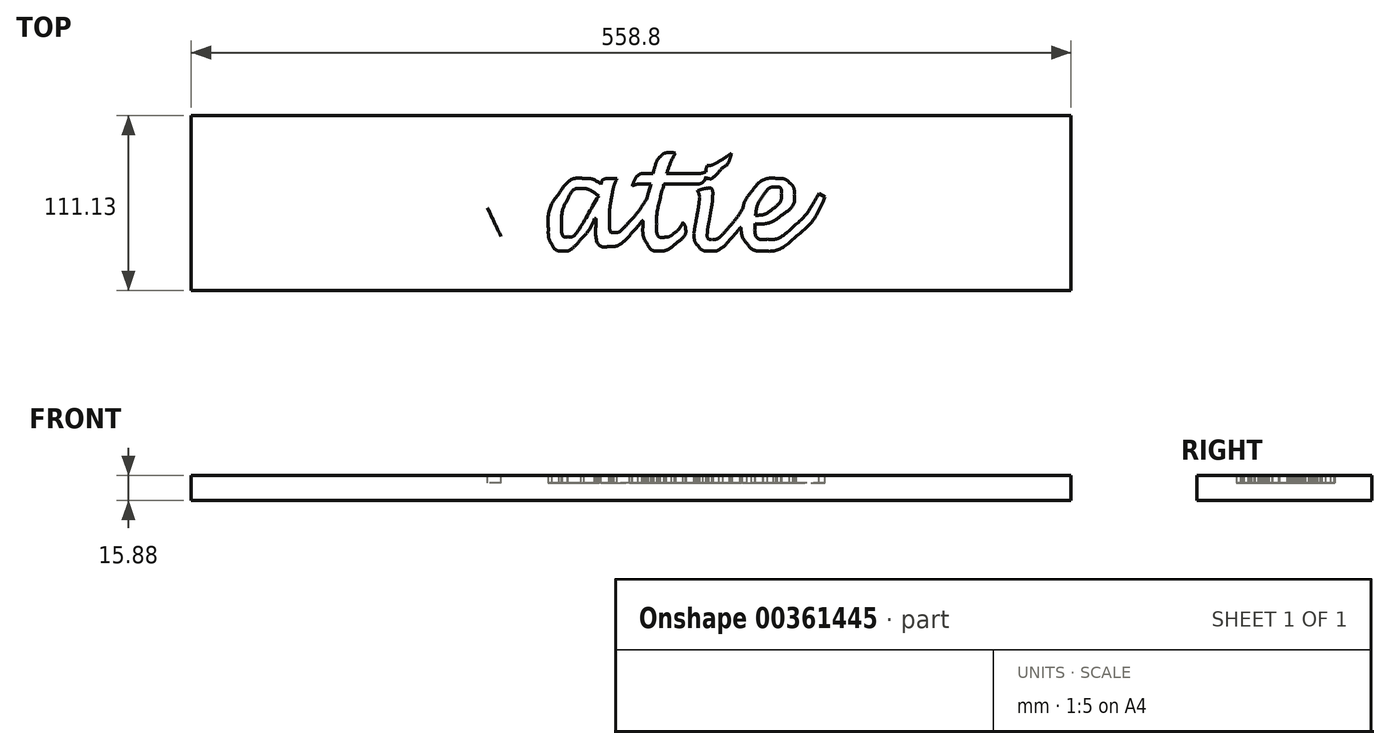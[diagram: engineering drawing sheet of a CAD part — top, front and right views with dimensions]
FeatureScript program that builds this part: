
annotation { "Feature Type Name" : "Feature", "Feature Type Description" : "" }
export const myFeature = defineFeature(function(context is Context, id is Id, definition is map)
    precondition{}
    {
        {
            var Q0;
            Q0=qCreatedBy(makeId("Top.planeOp"),FACE);
            var sketch = newSketch(context, id + "F0", { "sketchPlane" : qUnion([Q0])});
            skLineSegment(sketch, "E0.bottom", {"start": v(12.7, 0) * mm, "end": v(546.1, 0) * mm});
            skLineSegment(sketch, "E0.top", {"start": v(12.7, 609.6) * mm, "end": v(546.1, 609.6) * mm});
            skLineSegment(sketch, "E0.left", {"start": v(0, 12.7) * mm, "end": v(0, 596.9) * mm});
            skLineSegment(sketch, "E0.right", {"start": v(558.8, 12.7) * mm, "end": v(558.8, 596.9) * mm});
            skPoint(sketch, "E1.visualSharp", {"position": v(0, 609.6) * mm});
            skArc(sketch, "E1.filletArc", {"start": v(12.7, 609.6) * mm, "mid": v(3.72, 605.88) * mm, "end": v(0, 596.9) * mm});
            skPoint(sketch, "E2.visualSharp", {"position": v(0, 0) * mm});
            skArc(sketch, "E2.filletArc", {"start": v(0, 12.7) * mm, "mid": v(3.72, 3.72) * mm, "end": v(12.7, 0) * mm});
            skPoint(sketch, "E3.visualSharp", {"position": v(558.8, 0) * mm});
            skArc(sketch, "E3.filletArc", {"start": v(546.1, 0) * mm, "mid": v(555.08, 3.72) * mm, "end": v(558.8, 12.7) * mm});
            skPoint(sketch, "E4.visualSharp", {"position": v(558.8, 609.6) * mm});
            skArc(sketch, "E4.filletArc", {"start": v(558.8, 596.9) * mm, "mid": v(555.08, 605.88) * mm, "end": v(546.1, 609.6) * mm});
            skSolve(sketch);
        }
        {
            var Q0;
            Q0=makeQuery(id+"F0.imprint","IMPRINT",FACE,{"disambiguationData":[TD([[makeQuery(id+"F0.imprint","IMPRINT",EDGE,{"derivedFrom":sQuery(id+"F0.wireOp",EDGE,"E0.bottom")}),1.0]])]});
            extrude(context, id + "F1", {"entities" : qUnion([Q0]), "depth" : 15.88 * mm});
        }
        {
            var Q0;
            Q0=makeQuery(id+"F1.opExtrude","CAP_FACE",FACE,{"disambiguationData":[OSD([sQuery(id+"F0.wireOp",EDGE,"E0.bottom"),sQuery(id+"F0.wireOp",EDGE,"E0.top"),sQuery(id+"F0.wireOp",EDGE,"E0.left"),sQuery(id+"F0.wireOp",EDGE,"E0.right"),sQuery(id+"F0.wireOp",EDGE,"E1.filletArc"),sQuery(id+"F0.wireOp",EDGE,"E2.filletArc"),sQuery(id+"F0.wireOp",EDGE,"E3.filletArc"),sQuery(id+"F0.wireOp",EDGE,"E4.filletArc")])],"isStart":false});
            var sketch = newSketch(context, id + "F2", { "sketchPlane" : qUnion([Q0])});
            skFitSpline(sketch, "E5", {"points": [v(247.46, 485.02) * mm, v(244.22, 485.02) * mm, v(241.38, 482.73) * mm, v(238.94, 478.15) * mm]});
            skFitSpline(sketch, "E6", {"points": [v(238.94, 478.15) * mm, v(236.48, 473.56) * mm, v(235.26, 468.05) * mm, v(235.26, 461.6) * mm]});
            skFitSpline(sketch, "E7", {"points": [v(235.26, 461.6) * mm, v(235.26, 456.87) * mm, v(236.54, 454.5) * mm, v(239.12, 454.5) * mm]});
            skFitSpline(sketch, "E8", {"points": [v(239.12, 454.5) * mm, v(242.2, 454.5) * mm, v(248.34, 462.57) * mm, v(257.6, 478.7) * mm]});
            skFitSpline(sketch, "E9", {"points": [v(257.6, 478.7) * mm, v(257.73, 478.94) * mm, v(258.18, 479.46) * mm, v(258.91, 480.26) * mm]});
            skFitSpline(sketch, "E10", {"points": [v(258.91, 480.26) * mm, v(254.36, 483.44) * mm, v(250.54, 485.02) * mm, v(247.46, 485.02) * mm]});
            skFitSpline(sketch, "E11", {"points": [v(371.38, 485.98) * mm, v(368.47, 485.98) * mm, v(365.74, 484.16) * mm, v(363.18, 480.52) * mm]});
            skFitSpline(sketch, "E12", {"points": [v(363.18, 480.52) * mm, v(360.62, 476.88) * mm, v(359.03, 472.72) * mm, v(358.4, 468.06) * mm]});
            skFitSpline(sketch, "E13", {"points": [v(358.4, 468.06) * mm, v(362.59, 468.32) * mm, v(366.35, 469.82) * mm, v(369.66, 472.53) * mm]});
            skFitSpline(sketch, "E14", {"points": [v(369.66, 472.53) * mm, v(372.98, 475.24) * mm, v(374.64, 478.32) * mm, v(374.64, 481.78) * mm]});
            skFitSpline(sketch, "E15", {"points": [v(374.64, 481.78) * mm, v(374.64, 484.58) * mm, v(373.55, 485.98) * mm, v(371.38, 485.98) * mm]});
            skFitSpline(sketch, "E16", {"points": [v(372.25, 491.45) * mm, v(375.43, 491.45) * mm, v(378, 490.53) * mm, v(379.95, 488.68) * mm]});
            skFitSpline(sketch, "E17", {"points": [v(379.95, 488.68) * mm, v(381.9, 486.84) * mm, v(382.89, 484.38) * mm, v(382.89, 481.3) * mm]});
            skFitSpline(sketch, "E18", {"points": [v(382.89, 481.3) * mm, v(382.89, 476.36) * mm, v(380.3, 472.02) * mm, v(375.12, 468.3) * mm]});
            skFitSpline(sketch, "E19", {"points": [v(375.12, 468.3) * mm, v(369.94, 464.57) * mm, v(364.27, 462.7) * mm, v(358.12, 462.7) * mm]});
            skFitSpline(sketch, "E20", {"points": [v(358.12, 462.7) * mm, v(358.12, 456.15) * mm, v(360.76, 452.87) * mm, v(366.01, 452.87) * mm]});
            skFitSpline(sketch, "E21", {"points": [v(366.01, 452.87) * mm, v(370.84, 452.87) * mm, v(376.2, 455.49) * mm, v(382.13, 460.74) * mm]});
            skFitSpline(sketch, "E22", {"points": [v(382.13, 460.74) * mm, v(388.04, 465.98) * mm, v(393.52, 473.06) * mm, v(398.54, 481.95) * mm]});
            skFitSpline(sketch, "E23", {"points": [v(402.5, 479.62) * mm, v(397.84, 469.55) * mm, v(391.82, 461.33) * mm, v(384.42, 454.98) * mm]});
            skFitSpline(sketch, "E24", {"points": [v(384.42, 454.98) * mm, v(377.03, 448.62) * mm, v(369.98, 445.45) * mm, v(363.3, 445.45) * mm]});
            skFitSpline(sketch, "E25", {"points": [v(363.3, 445.45) * mm, v(358.9, 445.45) * mm, v(355.42, 447.05) * mm, v(352.87, 450.22) * mm]});
            skFitSpline(sketch, "E26", {"points": [v(352.87, 450.22) * mm, v(350.64, 453) * mm, v(349.4, 456.61) * mm, v(349.1, 461.08) * mm]});
            skFitSpline(sketch, "E27", {"points": [v(349.1, 461.08) * mm, v(347.32, 458.56) * mm, v(345.51, 456.33) * mm, v(343.7, 454.35) * mm]});
            skFitSpline(sketch, "E28", {"points": [v(343.7, 454.35) * mm, v(338.24, 448.42) * mm, v(333.27, 445.45) * mm, v(328.8, 445.45) * mm]});
            skFitSpline(sketch, "E29", {"points": [v(328.8, 445.45) * mm, v(325.99, 445.45) * mm, v(323.71, 446.48) * mm, v(322, 448.54) * mm]});
            skFitSpline(sketch, "E30", {"points": [v(322, 448.54) * mm, v(320.27, 450.6) * mm, v(319.41, 453.3) * mm, v(319.41, 456.62) * mm]});
            skFitSpline(sketch, "E31", {"points": [v(319.41, 456.62) * mm, v(319.41, 457.85) * mm, v(319.64, 459.77) * mm, v(320.12, 462.36) * mm]});
            skLineSegment(sketch, "E32", {"start": v(398.54, 481.95) * mm, "end": v(402.5, 479.62) * mm});
            skLineSegment(sketch, "E33", {"start": v(402.5, 479.62) * mm, "end": v(398.54, 481.95) * mm});
            skFitSpline(sketch, "E34", {"points": [v(320.89, 466.68) * mm, v(322, 472.85) * mm, v(322.57, 477.15) * mm, v(322.57, 479.6) * mm]});
            skFitSpline(sketch, "E35", {"points": [v(322.57, 479.6) * mm, v(322.57, 480.87) * mm, v(322.18, 482.24) * mm, v(321.4, 483.7) * mm]});
            skFitSpline(sketch, "E36", {"points": [v(321.4, 483.7) * mm, v(324.84, 484.7) * mm, v(326.97, 485.22) * mm, v(327.78, 485.22) * mm]});
            skFitSpline(sketch, "E37", {"points": [v(327.78, 485.22) * mm, v(329.99, 485.22) * mm, v(331.1, 483.6) * mm, v(331.1, 480.35) * mm]});
            skFitSpline(sketch, "E38", {"points": [v(331.1, 480.35) * mm, v(331.1, 478.32) * mm, v(330.76, 475.38) * mm, v(330.07, 471.54) * mm]});
            skLineSegment(sketch, "E39", {"start": v(320.12, 462.36) * mm, "end": v(320.89, 466.68) * mm});
            skLineSegment(sketch, "E40", {"start": v(320.89, 466.68) * mm, "end": v(320.12, 462.36) * mm});
            skFitSpline(sketch, "E41", {"points": [v(328.7, 463.92) * mm, v(328.05, 460.32) * mm, v(327.73, 458) * mm, v(327.73, 456.92) * mm]});
            skFitSpline(sketch, "E42", {"points": [v(327.73, 456.92) * mm, v(327.73, 454.22) * mm, v(328.7, 452.87) * mm, v(330.64, 452.87) * mm]});
            skFitSpline(sketch, "E43", {"points": [v(330.64, 452.87) * mm, v(333.34, 452.87) * mm, v(337.06, 455.56) * mm, v(341.8, 460.93) * mm]});
            skFitSpline(sketch, "E44", {"points": [v(341.8, 460.93) * mm, v(344.6, 464.12) * mm, v(347.4, 467.87) * mm, v(350.2, 472.2) * mm]});
            skFitSpline(sketch, "E45", {"points": [v(350.2, 472.2) * mm, v(351.28, 476.24) * mm, v(353.16, 479.88) * mm, v(355.83, 483.14) * mm]});
            skFitSpline(sketch, "E46", {"points": [v(355.83, 483.14) * mm, v(360.35, 488.68) * mm, v(365.83, 491.45) * mm, v(372.25, 491.45) * mm]});
            skLineSegment(sketch, "E47", {"start": v(330.07, 471.54) * mm, "end": v(328.7, 463.92) * mm});
            skLineSegment(sketch, "E48", {"start": v(328.7, 463.92) * mm, "end": v(330.07, 471.54) * mm});
            skFitSpline(sketch, "E49", {"points": [v(305.1, 507.84) * mm, v(305.33, 507.84) * mm, v(306.14, 507.78) * mm, v(307.5, 507.65) * mm]});
            skFitSpline(sketch, "E50", {"points": [v(307.5, 507.65) * mm, v(305.64, 504.33) * mm, v(303.76, 499.96) * mm, v(301.86, 494.56) * mm]});
            skFitSpline(sketch, "E51", {"points": [v(319.5, 494.56) * mm, v(322.22, 494.56) * mm, v(324.64, 494.92) * mm, v(326.74, 495.67) * mm]});
            skFitSpline(sketch, "E52", {"points": [v(326.74, 495.67) * mm, v(326.87, 497.05) * mm, v(327.2, 498.41) * mm, v(327.69, 499.77) * mm]});
            skLineSegment(sketch, "E53", {"start": v(301.86, 494.56) * mm, "end": v(319.5, 494.56) * mm});
            skLineSegment(sketch, "E54", {"start": v(319.5, 494.56) * mm, "end": v(301.86, 494.56) * mm});
            skFitSpline(sketch, "E55", {"points": [v(328.67, 499.72) * mm, v(330.08, 499.79) * mm, v(332.2, 500.64) * mm, v(335.04, 502.28) * mm]});
            skFitSpline(sketch, "E56", {"points": [v(335.04, 502.28) * mm, v(337.9, 503.93) * mm, v(340.52, 505.68) * mm, v(342.94, 507.52) * mm]});
            skFitSpline(sketch, "E57", {"points": [v(342.94, 507.52) * mm, v(341.85, 503.08) * mm, v(340.03, 500.06) * mm, v(337.5, 498.48) * mm]});
            skFitSpline(sketch, "E58", {"points": [v(337.5, 498.48) * mm, v(333.26, 493.7) * mm, v(330.34, 491.32) * mm, v(328.76, 491.32) * mm]});
            skFitSpline(sketch, "E59", {"points": [v(328.76, 491.32) * mm, v(327.76, 491.32) * mm, v(327.1, 491.79) * mm, v(326.85, 492.72) * mm]});
            skFitSpline(sketch, "E60", {"points": [v(326.85, 492.72) * mm, v(326.33, 491.05) * mm, v(325.73, 489.92) * mm, v(325.02, 489.33) * mm]});
            skFitSpline(sketch, "E61", {"points": [v(325.02, 489.33) * mm, v(323.92, 488.4) * mm, v(321.98, 487.93) * mm, v(319.18, 487.93) * mm]});
            skLineSegment(sketch, "E62", {"start": v(327.69, 499.77) * mm, "end": v(328.67, 499.72) * mm});
            skLineSegment(sketch, "E63", {"start": v(328.67, 499.72) * mm, "end": v(327.69, 499.77) * mm});
            skFitSpline(sketch, "E64", {"points": [v(300.17, 487.93) * mm, v(300.04, 487.44) * mm, v(299.9, 486.92) * mm, v(299.75, 486.38) * mm]});
            skFitSpline(sketch, "E65", {"points": [v(299.75, 486.38) * mm, v(296.99, 475.84) * mm, v(295.6, 467.88) * mm, v(295.6, 462.47) * mm]});
            skFitSpline(sketch, "E66", {"points": [v(295.6, 462.47) * mm, v(295.6, 456.94) * mm, v(297.3, 454.18) * mm, v(300.68, 454.18) * mm]});
            skFitSpline(sketch, "E67", {"points": [v(300.68, 454.18) * mm, v(302.53, 454.18) * mm, v(304.57, 455.1) * mm, v(306.8, 456.9) * mm]});
            skFitSpline(sketch, "E68", {"points": [v(306.8, 456.9) * mm, v(309.05, 458.71) * mm, v(310.85, 460.91) * mm, v(312.2, 463.5) * mm]});
            skFitSpline(sketch, "E69", {"points": [v(312.2, 463.5) * mm, v(313.35, 461.8) * mm, v(313.92, 460.42) * mm, v(313.92, 459.33) * mm]});
            skFitSpline(sketch, "E70", {"points": [v(313.92, 459.33) * mm, v(313.92, 456.5) * mm, v(311.92, 453.5) * mm, v(307.92, 450.28) * mm]});
            skFitSpline(sketch, "E71", {"points": [v(307.92, 450.28) * mm, v(303.9, 447.06) * mm, v(300.24, 445.45) * mm, v(296.9, 445.45) * mm]});
            skFitSpline(sketch, "E72", {"points": [v(296.9, 445.45) * mm, v(293.88, 445.45) * mm, v(291.42, 446.93) * mm, v(289.56, 449.9) * mm]});
            skFitSpline(sketch, "E73", {"points": [v(289.56, 449.9) * mm, v(287.7, 452.87) * mm, v(286.76, 456.65) * mm, v(286.76, 461.23) * mm]});
            skFitSpline(sketch, "E74", {"points": [v(286.76, 461.23) * mm, v(286.76, 462.58) * mm, v(286.84, 464.08) * mm, v(287.02, 465.75) * mm]});
            skFitSpline(sketch, "E75", {"points": [v(287.02, 465.75) * mm, v(284.81, 462.56) * mm, v(282.47, 459.69) * mm, v(280.01, 457.13) * mm]});
            skFitSpline(sketch, "E76", {"points": [v(280.01, 457.13) * mm, v(274.37, 451.28) * mm, v(269.48, 448.36) * mm, v(265.31, 448.36) * mm]});
            skFitSpline(sketch, "E77", {"points": [v(265.31, 448.36) * mm, v(259.81, 448.36) * mm, v(257.07, 453.3) * mm, v(257.07, 463.23) * mm]});
            skFitSpline(sketch, "E78", {"points": [v(257.07, 463.23) * mm, v(257.07, 465.2) * mm, v(257.14, 467.57) * mm, v(257.28, 470.32) * mm]});
            skFitSpline(sketch, "E79", {"points": [v(257.28, 470.32) * mm, v(255.19, 463.64) * mm, v(251.91, 457.83) * mm, v(247.46, 452.87) * mm]});
            skFitSpline(sketch, "E80", {"points": [v(247.46, 452.87) * mm, v(242.99, 447.92) * mm, v(239.04, 445.45) * mm, v(235.6, 445.45) * mm]});
            skFitSpline(sketch, "E81", {"points": [v(235.6, 445.45) * mm, v(232.88, 445.45) * mm, v(230.72, 446.77) * mm, v(229.15, 449.4) * mm]});
            skFitSpline(sketch, "E82", {"points": [v(229.15, 449.4) * mm, v(227.56, 452.05) * mm, v(226.77, 455.51) * mm, v(226.77, 459.78) * mm]});
            skFitSpline(sketch, "E83", {"points": [v(226.77, 459.78) * mm, v(226.77, 468.13) * mm, v(229.03, 475.5) * mm, v(233.56, 481.87) * mm]});
            skFitSpline(sketch, "E84", {"points": [v(233.56, 481.87) * mm, v(238.09, 488.26) * mm, v(243.35, 491.45) * mm, v(249.38, 491.45) * mm]});
            skFitSpline(sketch, "E85", {"points": [v(249.38, 491.45) * mm, v(253.01, 491.45) * mm, v(256.66, 490.21) * mm, v(260.33, 487.76) * mm]});
            skFitSpline(sketch, "E86", {"points": [v(260.33, 487.76) * mm, v(260.86, 490.19) * mm, v(263.48, 491.4) * mm, v(268.16, 491.4) * mm]});
            skFitSpline(sketch, "E87", {"points": [v(268.16, 491.4) * mm, v(268.26, 491.4) * mm, v(268.96, 491.37) * mm, v(270.27, 491.3) * mm]});
            skFitSpline(sketch, "E88", {"points": [v(270.27, 491.3) * mm, v(268.9, 488.33) * mm, v(267.89, 484.93) * mm, v(267.2, 481.1) * mm]});
            skLineSegment(sketch, "E89", {"start": v(319.18, 487.93) * mm, "end": v(300.17, 487.93) * mm});
            skLineSegment(sketch, "E90", {"start": v(300.17, 487.93) * mm, "end": v(319.18, 487.93) * mm});
            skFitSpline(sketch, "E91", {"points": [v(266.62, 477.77) * mm, v(265.96, 474.15) * mm, v(265.63, 469.88) * mm, v(265.63, 464.94) * mm]});
            skFitSpline(sketch, "E92", {"points": [v(265.63, 464.94) * mm, v(265.63, 459.77) * mm, v(266.57, 457.18) * mm, v(268.44, 457.18) * mm]});
            skFitSpline(sketch, "E93", {"points": [v(268.44, 457.18) * mm, v(270.76, 457.18) * mm, v(274.05, 459.48) * mm, v(278.32, 464.1) * mm]});
            skFitSpline(sketch, "E94", {"points": [v(278.32, 464.1) * mm, v(281.96, 468.04) * mm, v(285.66, 473) * mm, v(289.42, 478.98) * mm]});
            skFitSpline(sketch, "E95", {"points": [v(289.42, 478.98) * mm, v(289.7, 480.18) * mm, v(290, 481.4) * mm, v(290.32, 482.69) * mm]});
            skLineSegment(sketch, "E96", {"start": v(267.2, 481.1) * mm, "end": v(266.62, 477.77) * mm});
            skLineSegment(sketch, "E97", {"start": v(266.62, 477.77) * mm, "end": v(267.2, 481.1) * mm});
            skFitSpline(sketch, "E98", {"points": [v(286.65, 487.93) * mm, v(284.3, 487.93) * mm, v(282.1, 487.54) * mm, v(280.04, 486.76) * mm]});
            skFitSpline(sketch, "E99", {"points": [v(280.04, 486.76) * mm, v(281.5, 490.38) * mm, v(282.72, 492.6) * mm, v(283.72, 493.38) * mm]});
            skFitSpline(sketch, "E100", {"points": [v(283.72, 493.38) * mm, v(284.71, 494.16) * mm, v(286.34, 494.56) * mm, v(288.6, 494.56) * mm]});
            skLineSegment(sketch, "E101", {"start": v(290.32, 482.69) * mm, "end": v(291.82, 487.93) * mm});
            skLineSegment(sketch, "E102", {"start": v(291.82, 487.93) * mm, "end": v(286.65, 487.93) * mm});
            skFitSpline(sketch, "E103", {"points": [v(293.99, 497.12) * mm, v(295.02, 501) * mm, v(296.33, 503.76) * mm, v(297.95, 505.4) * mm]});
            skFitSpline(sketch, "E104", {"points": [v(297.95, 505.4) * mm, v(299.55, 507.03) * mm, v(301.94, 507.84) * mm, v(305.1, 507.84) * mm]});
            skLineSegment(sketch, "E105", {"start": v(288.6, 494.56) * mm, "end": v(293.33, 494.56) * mm});
            skLineSegment(sketch, "E106", {"start": v(293.33, 494.56) * mm, "end": v(293.99, 497.12) * mm});
            skFitSpline(sketch, "E107", {"points": [v(178.41, 506.2) * mm, v(181.96, 506.2) * mm, v(186.85, 506.6) * mm, v(193.08, 507.4) * mm]});
            skFitSpline(sketch, "E108", {"points": [v(188.04, 478.85) * mm, v(200.42, 488.81) * mm, v(207.85, 498.44) * mm, v(210.33, 507.7) * mm]});
            skFitSpline(sketch, "E109", {"points": [v(210.33, 507.7) * mm, v(214.42, 505.56) * mm, v(216.46, 503.26) * mm, v(216.46, 500.79) * mm]});
            skFitSpline(sketch, "E110", {"points": [v(216.46, 500.79) * mm, v(216.46, 499.37) * mm, v(213.98, 496.13) * mm, v(209, 491.1) * mm]});
            skFitSpline(sketch, "E111", {"points": [v(209, 491.1) * mm, v(204.02, 486.08) * mm, v(199.1, 481.73) * mm, v(194.23, 478.07) * mm]});
            skFitSpline(sketch, "E112", {"points": [v(194.23, 478.07) * mm, v(198.39, 469.54) * mm, v(202.46, 462.52) * mm, v(206.43, 457.03) * mm]});
            skFitSpline(sketch, "E113", {"points": [v(206.43, 457.03) * mm, v(210.4, 451.54) * mm, v(213.38, 448.8) * mm, v(215.37, 448.8) * mm]});
            skFitSpline(sketch, "E114", {"points": [v(215.37, 448.8) * mm, v(217.55, 448.8) * mm, v(220.39, 450.27) * mm, v(223.87, 453.22) * mm]});
            skLineSegment(sketch, "E115", {"start": v(193.08, 507.4) * mm, "end": v(188.41, 480.96) * mm});
            skLineSegment(sketch, "E116", {"start": v(188.41, 480.96) * mm, "end": v(193.08, 507.4) * mm});
            skFitSpline(sketch, "E117", {"points": [v(223.98, 451.1) * mm, v(223.98, 449.09) * mm, v(222.68, 446.98) * mm, v(220.08, 444.73) * mm]});
            skFitSpline(sketch, "E118", {"points": [v(220.08, 444.73) * mm, v(217.49, 442.5) * mm, v(214.96, 441.38) * mm, v(212.51, 441.38) * mm]});
            skFitSpline(sketch, "E119", {"points": [v(212.54, 441.4) * mm, v(206.33, 441.4) * mm, v(197.88, 452.52) * mm, v(187.21, 474.77) * mm]});
            skLineSegment(sketch, "E120", {"start": v(223.87, 453.22) * mm, "end": v(223.98, 451.1) * mm});
            skLineSegment(sketch, "E121", {"start": v(223.98, 451.1) * mm, "end": v(223.87, 453.22) * mm});
            skFitSpline(sketch, "E122", {"points": [v(183.9, 454.8) * mm, v(183.48, 452.44) * mm, v(183.27, 450.88) * mm, v(183.27, 450.14) * mm]});
            skFitSpline(sketch, "E123", {"points": [v(183.27, 450.14) * mm, v(183.27, 449.5) * mm, v(183.42, 448.6) * mm, v(183.73, 447.42) * mm]});
            skFitSpline(sketch, "E124", {"points": [v(183.73, 447.42) * mm, v(180.96, 445.82) * mm, v(178.55, 445.01) * mm, v(176.52, 445.01) * mm]});
            skFitSpline(sketch, "E125", {"points": [v(176.52, 445.01) * mm, v(174.84, 445.01) * mm, v(174, 445.83) * mm, v(174, 447.45) * mm]});
            skFitSpline(sketch, "E126", {"points": [v(174, 447.45) * mm, v(174, 448.08) * mm, v(174.25, 449.8) * mm, v(174.74, 452.56) * mm]});
            skLineSegment(sketch, "E127", {"start": v(186.79, 472.34) * mm, "end": v(183.9, 454.8) * mm});
            skLineSegment(sketch, "E128", {"start": v(183.9, 454.8) * mm, "end": v(186.79, 472.34) * mm});
            skFitSpline(sketch, "E129", {"points": [v(183.17, 499.25) * mm, v(181.66, 498.94) * mm, v(180, 498.79) * mm, v(178.17, 498.79) * mm]});
            skFitSpline(sketch, "E130", {"points": [v(178.17, 498.79) * mm, v(174.1, 498.79) * mm, v(171.7, 502.02) * mm, v(170.94, 508.51) * mm]});
            skLineSegment(sketch, "E131", {"start": v(174.74, 452.56) * mm, "end": v(183.17, 499.25) * mm});
            skLineSegment(sketch, "E132", {"start": v(183.17, 499.25) * mm, "end": v(174.74, 452.56) * mm});
            skFitSpline(sketch, "E133", {"points": [v(247.46, 485.02) * mm, v(244.22, 485.02) * mm, v(241.38, 482.73) * mm, v(238.94, 478.15) * mm]});
            skFitSpline(sketch, "E134", {"points": [v(238.94, 478.15) * mm, v(236.48, 473.56) * mm, v(235.26, 468.05) * mm, v(235.26, 461.6) * mm]});
            skFitSpline(sketch, "E135", {"points": [v(235.26, 461.6) * mm, v(235.26, 456.87) * mm, v(236.54, 454.5) * mm, v(239.12, 454.5) * mm]});
            skFitSpline(sketch, "E136", {"points": [v(239.12, 454.5) * mm, v(242.2, 454.5) * mm, v(248.34, 462.57) * mm, v(257.6, 478.7) * mm]});
            skFitSpline(sketch, "E137", {"points": [v(257.6, 478.7) * mm, v(257.73, 478.94) * mm, v(258.18, 479.46) * mm, v(258.91, 480.26) * mm]});
            skFitSpline(sketch, "E138", {"points": [v(258.91, 480.26) * mm, v(254.36, 483.44) * mm, v(250.54, 485.02) * mm, v(247.46, 485.02) * mm]});
            skFitSpline(sketch, "E139", {"points": [v(371.38, 485.98) * mm, v(368.47, 485.98) * mm, v(365.74, 484.16) * mm, v(363.18, 480.52) * mm]});
            skFitSpline(sketch, "E140", {"points": [v(363.18, 480.52) * mm, v(360.62, 476.88) * mm, v(359.03, 472.72) * mm, v(358.4, 468.06) * mm]});
            skFitSpline(sketch, "E141", {"points": [v(358.4, 468.06) * mm, v(362.59, 468.32) * mm, v(366.35, 469.82) * mm, v(369.66, 472.53) * mm]});
            skFitSpline(sketch, "E142", {"points": [v(369.66, 472.53) * mm, v(372.98, 475.24) * mm, v(374.64, 478.32) * mm, v(374.64, 481.78) * mm]});
            skFitSpline(sketch, "E143", {"points": [v(374.64, 481.78) * mm, v(374.64, 484.58) * mm, v(373.55, 485.98) * mm, v(371.38, 485.98) * mm]});
            skFitSpline(sketch, "E144", {"points": [v(372.25, 491.45) * mm, v(375.43, 491.45) * mm, v(378, 490.53) * mm, v(379.95, 488.68) * mm]});
            skFitSpline(sketch, "E145", {"points": [v(379.95, 488.68) * mm, v(381.9, 486.84) * mm, v(382.89, 484.38) * mm, v(382.89, 481.3) * mm]});
            skFitSpline(sketch, "E146", {"points": [v(382.89, 481.3) * mm, v(382.89, 476.36) * mm, v(380.3, 472.02) * mm, v(375.12, 468.3) * mm]});
            skFitSpline(sketch, "E147", {"points": [v(375.12, 468.3) * mm, v(369.94, 464.57) * mm, v(364.27, 462.7) * mm, v(358.12, 462.7) * mm]});
            skFitSpline(sketch, "E148", {"points": [v(358.12, 462.7) * mm, v(358.12, 456.15) * mm, v(360.76, 452.87) * mm, v(366.01, 452.87) * mm]});
            skFitSpline(sketch, "E149", {"points": [v(366.01, 452.87) * mm, v(370.84, 452.87) * mm, v(376.2, 455.49) * mm, v(382.13, 460.74) * mm]});
            skFitSpline(sketch, "E150", {"points": [v(382.13, 460.74) * mm, v(388.04, 465.98) * mm, v(393.52, 473.06) * mm, v(398.54, 481.95) * mm]});
            skFitSpline(sketch, "E151", {"points": [v(402.5, 479.62) * mm, v(397.84, 469.55) * mm, v(391.82, 461.33) * mm, v(384.42, 454.98) * mm]});
            skFitSpline(sketch, "E152", {"points": [v(384.42, 454.98) * mm, v(377.03, 448.62) * mm, v(369.98, 445.45) * mm, v(363.3, 445.45) * mm]});
            skFitSpline(sketch, "E153", {"points": [v(363.3, 445.45) * mm, v(358.9, 445.45) * mm, v(355.42, 447.05) * mm, v(352.87, 450.22) * mm]});
            skFitSpline(sketch, "E154", {"points": [v(352.87, 450.22) * mm, v(350.64, 453) * mm, v(349.4, 456.61) * mm, v(349.1, 461.08) * mm]});
            skFitSpline(sketch, "E155", {"points": [v(349.1, 461.08) * mm, v(347.32, 458.56) * mm, v(345.51, 456.33) * mm, v(343.7, 454.35) * mm]});
            skFitSpline(sketch, "E156", {"points": [v(343.7, 454.35) * mm, v(338.24, 448.42) * mm, v(333.27, 445.45) * mm, v(328.8, 445.45) * mm]});
            skFitSpline(sketch, "E157", {"points": [v(328.8, 445.45) * mm, v(325.99, 445.45) * mm, v(323.71, 446.48) * mm, v(322, 448.54) * mm]});
            skFitSpline(sketch, "E158", {"points": [v(322, 448.54) * mm, v(320.27, 450.6) * mm, v(319.41, 453.3) * mm, v(319.41, 456.62) * mm]});
            skFitSpline(sketch, "E159", {"points": [v(319.41, 456.62) * mm, v(319.41, 457.85) * mm, v(319.64, 459.77) * mm, v(320.12, 462.36) * mm]});
            skFitSpline(sketch, "E160", {"points": [v(320.89, 466.68) * mm, v(322, 472.85) * mm, v(322.57, 477.15) * mm, v(322.57, 479.6) * mm]});
            skFitSpline(sketch, "E161", {"points": [v(322.57, 479.6) * mm, v(322.57, 480.87) * mm, v(322.18, 482.24) * mm, v(321.4, 483.7) * mm]});
            skFitSpline(sketch, "E162", {"points": [v(321.4, 483.7) * mm, v(324.84, 484.7) * mm, v(326.97, 485.22) * mm, v(327.78, 485.22) * mm]});
            skFitSpline(sketch, "E163", {"points": [v(327.78, 485.22) * mm, v(329.99, 485.22) * mm, v(331.1, 483.6) * mm, v(331.1, 480.35) * mm]});
            skFitSpline(sketch, "E164", {"points": [v(331.1, 480.35) * mm, v(331.1, 478.32) * mm, v(330.76, 475.38) * mm, v(330.07, 471.54) * mm]});
            skFitSpline(sketch, "E165", {"points": [v(328.7, 463.92) * mm, v(328.05, 460.32) * mm, v(327.73, 458) * mm, v(327.73, 456.92) * mm]});
            skFitSpline(sketch, "E166", {"points": [v(327.73, 456.92) * mm, v(327.73, 454.22) * mm, v(328.7, 452.87) * mm, v(330.64, 452.87) * mm]});
            skFitSpline(sketch, "E167", {"points": [v(330.64, 452.87) * mm, v(333.34, 452.87) * mm, v(337.06, 455.56) * mm, v(341.8, 460.93) * mm]});
            skFitSpline(sketch, "E168", {"points": [v(341.8, 460.93) * mm, v(344.6, 464.12) * mm, v(347.4, 467.87) * mm, v(350.2, 472.2) * mm]});
            skFitSpline(sketch, "E169", {"points": [v(350.2, 472.2) * mm, v(351.28, 476.24) * mm, v(353.16, 479.88) * mm, v(355.83, 483.14) * mm]});
            skFitSpline(sketch, "E170", {"points": [v(355.83, 483.14) * mm, v(360.35, 488.68) * mm, v(365.83, 491.45) * mm, v(372.25, 491.45) * mm]});
            skFitSpline(sketch, "E171", {"points": [v(305.1, 507.84) * mm, v(305.33, 507.84) * mm, v(306.14, 507.78) * mm, v(307.5, 507.65) * mm]});
            skFitSpline(sketch, "E172", {"points": [v(307.5, 507.65) * mm, v(305.64, 504.33) * mm, v(303.76, 499.96) * mm, v(301.86, 494.56) * mm]});
            skFitSpline(sketch, "E173", {"points": [v(319.5, 494.56) * mm, v(322.22, 494.56) * mm, v(324.64, 494.92) * mm, v(326.74, 495.67) * mm]});
            skFitSpline(sketch, "E174", {"points": [v(326.74, 495.67) * mm, v(326.87, 497.05) * mm, v(327.2, 498.41) * mm, v(327.69, 499.77) * mm]});
            skFitSpline(sketch, "E175", {"points": [v(328.67, 499.72) * mm, v(330.08, 499.79) * mm, v(332.2, 500.64) * mm, v(335.04, 502.28) * mm]});
            skFitSpline(sketch, "E176", {"points": [v(335.04, 502.28) * mm, v(337.9, 503.93) * mm, v(340.52, 505.68) * mm, v(342.94, 507.52) * mm]});
            skFitSpline(sketch, "E177", {"points": [v(342.94, 507.52) * mm, v(341.85, 503.08) * mm, v(340.03, 500.06) * mm, v(337.5, 498.48) * mm]});
            skFitSpline(sketch, "E178", {"points": [v(337.5, 498.48) * mm, v(333.26, 493.7) * mm, v(330.34, 491.32) * mm, v(328.76, 491.32) * mm]});
            skFitSpline(sketch, "E179", {"points": [v(328.76, 491.32) * mm, v(327.76, 491.32) * mm, v(327.1, 491.79) * mm, v(326.85, 492.72) * mm]});
            skFitSpline(sketch, "E180", {"points": [v(326.85, 492.72) * mm, v(326.33, 491.05) * mm, v(325.73, 489.92) * mm, v(325.02, 489.33) * mm]});
            skFitSpline(sketch, "E181", {"points": [v(325.02, 489.33) * mm, v(323.92, 488.4) * mm, v(321.98, 487.93) * mm, v(319.18, 487.93) * mm]});
            skFitSpline(sketch, "E182", {"points": [v(300.17, 487.93) * mm, v(300.04, 487.44) * mm, v(299.9, 486.92) * mm, v(299.75, 486.38) * mm]});
            skFitSpline(sketch, "E183", {"points": [v(299.75, 486.38) * mm, v(296.99, 475.84) * mm, v(295.6, 467.88) * mm, v(295.6, 462.47) * mm]});
            skFitSpline(sketch, "E184", {"points": [v(295.6, 462.47) * mm, v(295.6, 456.94) * mm, v(297.3, 454.18) * mm, v(300.68, 454.18) * mm]});
            skFitSpline(sketch, "E185", {"points": [v(300.68, 454.18) * mm, v(302.53, 454.18) * mm, v(304.57, 455.1) * mm, v(306.8, 456.9) * mm]});
            skFitSpline(sketch, "E186", {"points": [v(306.8, 456.9) * mm, v(309.05, 458.71) * mm, v(310.85, 460.91) * mm, v(312.2, 463.5) * mm]});
            skFitSpline(sketch, "E187", {"points": [v(312.2, 463.5) * mm, v(313.35, 461.8) * mm, v(313.92, 460.42) * mm, v(313.92, 459.33) * mm]});
            skFitSpline(sketch, "E188", {"points": [v(313.92, 459.33) * mm, v(313.92, 456.5) * mm, v(311.92, 453.5) * mm, v(307.92, 450.28) * mm]});
            skFitSpline(sketch, "E189", {"points": [v(307.92, 450.28) * mm, v(303.9, 447.06) * mm, v(300.24, 445.45) * mm, v(296.9, 445.45) * mm]});
            skFitSpline(sketch, "E190", {"points": [v(296.9, 445.45) * mm, v(293.88, 445.45) * mm, v(291.42, 446.93) * mm, v(289.56, 449.9) * mm]});
            skFitSpline(sketch, "E191", {"points": [v(289.56, 449.9) * mm, v(287.7, 452.87) * mm, v(286.76, 456.65) * mm, v(286.76, 461.23) * mm]});
            skFitSpline(sketch, "E192", {"points": [v(286.76, 461.23) * mm, v(286.76, 462.58) * mm, v(286.84, 464.08) * mm, v(287.02, 465.75) * mm]});
            skFitSpline(sketch, "E193", {"points": [v(287.02, 465.75) * mm, v(284.81, 462.56) * mm, v(282.47, 459.69) * mm, v(280.01, 457.13) * mm]});
            skFitSpline(sketch, "E194", {"points": [v(280.01, 457.13) * mm, v(274.37, 451.28) * mm, v(269.48, 448.36) * mm, v(265.31, 448.36) * mm]});
            skFitSpline(sketch, "E195", {"points": [v(265.31, 448.36) * mm, v(259.81, 448.36) * mm, v(257.07, 453.3) * mm, v(257.07, 463.23) * mm]});
            skFitSpline(sketch, "E196", {"points": [v(257.07, 463.23) * mm, v(257.07, 465.2) * mm, v(257.14, 467.57) * mm, v(257.28, 470.32) * mm]});
            skFitSpline(sketch, "E197", {"points": [v(257.28, 470.32) * mm, v(255.19, 463.64) * mm, v(251.91, 457.83) * mm, v(247.46, 452.87) * mm]});
            skFitSpline(sketch, "E198", {"points": [v(247.46, 452.87) * mm, v(242.99, 447.92) * mm, v(239.04, 445.45) * mm, v(235.6, 445.45) * mm]});
            skFitSpline(sketch, "E199", {"points": [v(235.6, 445.45) * mm, v(232.88, 445.45) * mm, v(230.72, 446.77) * mm, v(229.15, 449.4) * mm]});
            skFitSpline(sketch, "E200", {"points": [v(229.15, 449.4) * mm, v(227.56, 452.05) * mm, v(226.77, 455.51) * mm, v(226.77, 459.78) * mm]});
            skFitSpline(sketch, "E201", {"points": [v(226.77, 459.78) * mm, v(226.77, 468.13) * mm, v(229.03, 475.5) * mm, v(233.56, 481.87) * mm]});
            skFitSpline(sketch, "E202", {"points": [v(233.56, 481.87) * mm, v(238.09, 488.26) * mm, v(243.35, 491.45) * mm, v(249.38, 491.45) * mm]});
            skFitSpline(sketch, "E203", {"points": [v(249.38, 491.45) * mm, v(253.01, 491.45) * mm, v(256.66, 490.21) * mm, v(260.33, 487.76) * mm]});
            skFitSpline(sketch, "E204", {"points": [v(260.33, 487.76) * mm, v(260.86, 490.19) * mm, v(263.48, 491.4) * mm, v(268.16, 491.4) * mm]});
            skFitSpline(sketch, "E205", {"points": [v(268.16, 491.4) * mm, v(268.26, 491.4) * mm, v(268.96, 491.37) * mm, v(270.27, 491.3) * mm]});
            skFitSpline(sketch, "E206", {"points": [v(270.27, 491.3) * mm, v(268.9, 488.33) * mm, v(267.89, 484.93) * mm, v(267.2, 481.1) * mm]});
            skFitSpline(sketch, "E207", {"points": [v(266.62, 477.77) * mm, v(265.96, 474.15) * mm, v(265.63, 469.88) * mm, v(265.63, 464.94) * mm]});
            skFitSpline(sketch, "E208", {"points": [v(265.63, 464.94) * mm, v(265.63, 459.77) * mm, v(266.57, 457.18) * mm, v(268.44, 457.18) * mm]});
            skFitSpline(sketch, "E209", {"points": [v(268.44, 457.18) * mm, v(270.76, 457.18) * mm, v(274.05, 459.48) * mm, v(278.32, 464.1) * mm]});
            skFitSpline(sketch, "E210", {"points": [v(278.32, 464.1) * mm, v(281.96, 468.04) * mm, v(285.66, 473) * mm, v(289.42, 478.98) * mm]});
            skFitSpline(sketch, "E211", {"points": [v(289.42, 478.98) * mm, v(289.7, 480.18) * mm, v(290, 481.4) * mm, v(290.32, 482.69) * mm]});
            skFitSpline(sketch, "E212", {"points": [v(286.65, 487.93) * mm, v(284.3, 487.93) * mm, v(282.1, 487.54) * mm, v(280.04, 486.76) * mm]});
            skFitSpline(sketch, "E213", {"points": [v(280.04, 486.76) * mm, v(281.5, 490.38) * mm, v(282.72, 492.6) * mm, v(283.72, 493.38) * mm]});
            skFitSpline(sketch, "E214", {"points": [v(283.72, 493.38) * mm, v(284.71, 494.16) * mm, v(286.34, 494.56) * mm, v(288.6, 494.56) * mm]});
            skFitSpline(sketch, "E215", {"points": [v(293.99, 497.12) * mm, v(295.02, 501) * mm, v(296.33, 503.76) * mm, v(297.95, 505.4) * mm]});
            skFitSpline(sketch, "E216", {"points": [v(297.95, 505.4) * mm, v(299.55, 507.03) * mm, v(301.94, 507.84) * mm, v(305.1, 507.84) * mm]});
            skFitSpline(sketch, "E217", {"points": [v(170.94, 508.51) * mm, v(173.27, 506.97) * mm, v(175.75, 506.2) * mm, v(178.41, 506.2) * mm]});
            skFitSpline(sketch, "E218", {"points": [v(178.41, 506.2) * mm, v(181.96, 506.2) * mm, v(186.85, 506.6) * mm, v(193.08, 507.4) * mm]});
            skFitSpline(sketch, "E219", {"points": [v(188.04, 478.85) * mm, v(200.42, 488.81) * mm, v(207.85, 498.44) * mm, v(210.33, 507.7) * mm]});
            skFitSpline(sketch, "E220", {"points": [v(210.33, 507.7) * mm, v(214.42, 505.56) * mm, v(216.46, 503.26) * mm, v(216.46, 500.79) * mm]});
            skFitSpline(sketch, "E221", {"points": [v(216.46, 500.79) * mm, v(216.46, 499.37) * mm, v(213.98, 496.13) * mm, v(209, 491.1) * mm]});
            skFitSpline(sketch, "E222", {"points": [v(209, 491.1) * mm, v(204.02, 486.08) * mm, v(199.1, 481.73) * mm, v(194.23, 478.07) * mm]});
            skFitSpline(sketch, "E223", {"points": [v(194.23, 478.07) * mm, v(198.39, 469.54) * mm, v(202.46, 462.52) * mm, v(206.43, 457.03) * mm]});
            skFitSpline(sketch, "E224", {"points": [v(206.43, 457.03) * mm, v(210.4, 451.54) * mm, v(213.38, 448.8) * mm, v(215.37, 448.8) * mm]});
            skFitSpline(sketch, "E225", {"points": [v(215.37, 448.8) * mm, v(217.55, 448.8) * mm, v(220.39, 450.27) * mm, v(223.87, 453.22) * mm]});
            skFitSpline(sketch, "E226", {"points": [v(223.98, 451.1) * mm, v(223.98, 449.09) * mm, v(222.68, 446.98) * mm, v(220.08, 444.73) * mm]});
            skFitSpline(sketch, "E227", {"points": [v(220.08, 444.73) * mm, v(217.49, 442.5) * mm, v(214.96, 441.38) * mm, v(212.51, 441.38) * mm]});
            skFitSpline(sketch, "E228", {"points": [v(212.51, 441.38) * mm, v(206.3, 441.4) * mm, v(197.87, 452.53) * mm, v(187.24, 474.8) * mm]});
            skFitSpline(sketch, "E229", {"points": [v(183.9, 454.8) * mm, v(183.48, 452.44) * mm, v(183.27, 450.88) * mm, v(183.27, 450.14) * mm]});
            skFitSpline(sketch, "E230", {"points": [v(183.27, 450.14) * mm, v(183.27, 449.5) * mm, v(183.42, 448.6) * mm, v(183.73, 447.42) * mm]});
            skFitSpline(sketch, "E231", {"points": [v(183.73, 447.42) * mm, v(180.96, 445.82) * mm, v(178.55, 445.01) * mm, v(176.52, 445.01) * mm]});
            skFitSpline(sketch, "E232", {"points": [v(176.52, 445.01) * mm, v(174.84, 445.01) * mm, v(174, 445.83) * mm, v(174, 447.45) * mm]});
            skFitSpline(sketch, "E233", {"points": [v(174, 447.45) * mm, v(174, 448.08) * mm, v(174.25, 449.8) * mm, v(174.74, 452.56) * mm]});
            skFitSpline(sketch, "E234", {"points": [v(183.17, 499.25) * mm, v(181.66, 498.94) * mm, v(180, 498.79) * mm, v(178.17, 498.79) * mm]});
            skFitSpline(sketch, "E235", {"points": [v(178.17, 498.79) * mm, v(174.1, 498.79) * mm, v(171.7, 502.02) * mm, v(170.94, 508.51) * mm]});
            skFitSpline(sketch, "E236", {"points": [v(277.79, 394.65) * mm, v(280.95, 394.65) * mm, v(283.67, 394.04) * mm, v(285.93, 392.83) * mm]});
            skFitSpline(sketch, "E237", {"points": [v(285.93, 392.83) * mm, v(288.2, 391.61) * mm, v(289.33, 390.05) * mm, v(289.33, 388.1) * mm]});
            skFitSpline(sketch, "E238", {"points": [v(289.33, 388.1) * mm, v(289.33, 386.55) * mm, v(288.3, 384.9) * mm, v(286.28, 383.13) * mm]});
            skFitSpline(sketch, "E239", {"points": [v(286.28, 383.13) * mm, v(284.16, 387.16) * mm, v(281.01, 389.18) * mm, v(276.84, 389.18) * mm]});
            skFitSpline(sketch, "E240", {"points": [v(276.84, 389.18) * mm, v(274.08, 389.18) * mm, v(271.82, 388.38) * mm, v(270.07, 386.75) * mm]});
            skFitSpline(sketch, "E241", {"points": [v(270.07, 386.75) * mm, v(268.32, 385.12) * mm, v(267.44, 383.06) * mm, v(267.44, 380.56) * mm]});
            skFitSpline(sketch, "E242", {"points": [v(267.44, 380.56) * mm, v(267.44, 377.66) * mm, v(268.8, 375.02) * mm, v(271.5, 372.69) * mm]});
            skFitSpline(sketch, "E243", {"points": [v(271.5, 372.69) * mm, v(273.4, 373.18) * mm, v(275.11, 373.43) * mm, v(276.63, 373.43) * mm]});
            skFitSpline(sketch, "E244", {"points": [v(276.63, 373.43) * mm, v(278.07, 373.43) * mm, v(279.73, 373.08) * mm, v(281.63, 372.4) * mm]});
            skFitSpline(sketch, "E245", {"points": [v(281.63, 372.4) * mm, v(280.16, 367.34) * mm, v(277.58, 364.81) * mm, v(273.88, 364.81) * mm]});
            skFitSpline(sketch, "E246", {"points": [v(273.88, 364.81) * mm, v(272.36, 364.81) * mm, v(270.86, 365.22) * mm, v(269.35, 366.02) * mm]});
            skFitSpline(sketch, "E247", {"points": [v(269.35, 366.02) * mm, v(265.7, 364.5) * mm, v(262.72, 362.19) * mm, v(260.42, 359.13) * mm]});
            skFitSpline(sketch, "E248", {"points": [v(260.42, 359.13) * mm, v(258.12, 356.06) * mm, v(256.96, 352.8) * mm, v(256.96, 349.32) * mm]});
            skFitSpline(sketch, "E249", {"points": [v(256.96, 349.32) * mm, v(256.96, 346.25) * mm, v(258.1, 343.74) * mm, v(260.39, 341.8) * mm]});
            skFitSpline(sketch, "E250", {"points": [v(260.39, 341.8) * mm, v(262.67, 339.86) * mm, v(265.66, 338.88) * mm, v(269.4, 338.88) * mm]});
            skFitSpline(sketch, "E251", {"points": [v(269.4, 338.88) * mm, v(273.9, 338.88) * mm, v(278.46, 340.78) * mm, v(283.03, 344.56) * mm]});
            skFitSpline(sketch, "E252", {"points": [v(283.03, 344.56) * mm, v(287.61, 348.33) * mm, v(289.9, 352.03) * mm, v(289.9, 355.63) * mm]});
            skFitSpline(sketch, "E253", {"points": [v(289.9, 355.63) * mm, v(289.9, 357.33) * mm, v(289.16, 358.57) * mm, v(287.7, 359.33) * mm]});
            skFitSpline(sketch, "E254", {"points": [v(286.49, 359.8) * mm, v(285.1, 360.5) * mm, v(284.39, 361.54) * mm, v(284.39, 362.92) * mm]});
            skFitSpline(sketch, "E255", {"points": [v(284.39, 362.92) * mm, v(284.39, 364.24) * mm, v(284.98, 366.15) * mm, v(286.17, 368.6) * mm]});
            skFitSpline(sketch, "E256", {"points": [v(286.17, 368.6) * mm, v(289.42, 367.14) * mm, v(293.87, 366.41) * mm, v(299.52, 366.41) * mm]});
            skFitSpline(sketch, "E257", {"points": [v(299.52, 366.41) * mm, v(302.52, 366.41) * mm, v(305.82, 366.82) * mm, v(309.44, 367.62) * mm]});
            skFitSpline(sketch, "E258", {"points": [v(309.44, 367.62) * mm, v(308.5, 363.93) * mm, v(307.32, 361.5) * mm, v(305.9, 360.33) * mm]});
            skFitSpline(sketch, "E259", {"points": [v(305.9, 360.33) * mm, v(304.46, 359.17) * mm, v(302.3, 358.6) * mm, v(299.4, 358.6) * mm]});
            skFitSpline(sketch, "E260", {"points": [v(299.4, 358.6) * mm, v(298.84, 358.6) * mm, v(298.17, 358.64) * mm, v(297.4, 358.75) * mm]});
            skFitSpline(sketch, "E261", {"points": [v(297.4, 358.75) * mm, v(294.74, 350.17) * mm, v(293.41, 343.18) * mm, v(293.41, 337.77) * mm]});
            skFitSpline(sketch, "E262", {"points": [v(293.41, 337.77) * mm, v(293.41, 333.72) * mm, v(294.08, 330.44) * mm, v(295.4, 327.95) * mm]});
            skFitSpline(sketch, "E263", {"points": [v(295.4, 327.95) * mm, v(293.52, 325.82) * mm, v(291.53, 324.77) * mm, v(289.43, 324.77) * mm]});
            skFitSpline(sketch, "E264", {"points": [v(289.43, 324.77) * mm, v(287.44, 324.77) * mm, v(286.45, 326.37) * mm, v(286.45, 329.58) * mm]});
            skFitSpline(sketch, "E265", {"points": [v(286.45, 329.58) * mm, v(286.45, 332.7) * mm, v(287.06, 337.43) * mm, v(288.26, 343.75) * mm]});
            skFitSpline(sketch, "E266", {"points": [v(288.26, 343.75) * mm, v(282.52, 336.1) * mm, v(275.37, 332.25) * mm, v(266.85, 332.25) * mm]});
            skFitSpline(sketch, "E267", {"points": [v(266.85, 332.25) * mm, v(261.33, 332.25) * mm, v(256.9, 333.76) * mm, v(253.56, 336.78) * mm]});
            skFitSpline(sketch, "E268", {"points": [v(253.56, 336.78) * mm, v(250.21, 339.8) * mm, v(248.55, 343.84) * mm, v(248.55, 348.92) * mm]});
            skFitSpline(sketch, "E269", {"points": [v(248.55, 348.92) * mm, v(248.55, 358.85) * mm, v(254.08, 365.7) * mm, v(265.16, 369.52) * mm]});
            skFitSpline(sketch, "E270", {"points": [v(265.16, 369.52) * mm, v(261.45, 371.14) * mm, v(259.6, 374.46) * mm, v(259.6, 379.46) * mm]});
            skFitSpline(sketch, "E271", {"points": [v(259.6, 379.46) * mm, v(259.6, 383.85) * mm, v(261.34, 387.47) * mm, v(264.82, 390.34) * mm]});
            skFitSpline(sketch, "E272", {"points": [v(264.82, 390.34) * mm, v(268.3, 393.21) * mm, v(272.62, 394.65) * mm, v(277.79, 394.65) * mm]});
            skLineSegment(sketch, "E273", {"start": v(287.7, 359.33) * mm, "end": v(286.49, 359.8) * mm});
            skLineSegment(sketch, "E274", {"start": v(286.49, 359.8) * mm, "end": v(287.7, 359.33) * mm});
            skFitSpline(sketch, "E275", {"points": [v(277.79, 394.65) * mm, v(280.95, 394.65) * mm, v(283.67, 394.04) * mm, v(285.93, 392.83) * mm]});
            skFitSpline(sketch, "E276", {"points": [v(285.93, 392.83) * mm, v(288.2, 391.61) * mm, v(289.33, 390.05) * mm, v(289.33, 388.1) * mm]});
            skFitSpline(sketch, "E277", {"points": [v(289.33, 388.1) * mm, v(289.33, 386.55) * mm, v(288.3, 384.9) * mm, v(286.28, 383.13) * mm]});
            skFitSpline(sketch, "E278", {"points": [v(286.28, 383.13) * mm, v(284.16, 387.16) * mm, v(281.01, 389.18) * mm, v(276.84, 389.18) * mm]});
            skFitSpline(sketch, "E279", {"points": [v(276.84, 389.18) * mm, v(274.08, 389.18) * mm, v(271.82, 388.38) * mm, v(270.07, 386.75) * mm]});
            skFitSpline(sketch, "E280", {"points": [v(270.07, 386.75) * mm, v(268.32, 385.12) * mm, v(267.44, 383.06) * mm, v(267.44, 380.56) * mm]});
            skFitSpline(sketch, "E281", {"points": [v(267.44, 380.56) * mm, v(267.44, 377.66) * mm, v(268.8, 375.02) * mm, v(271.5, 372.69) * mm]});
            skFitSpline(sketch, "E282", {"points": [v(271.5, 372.69) * mm, v(273.4, 373.18) * mm, v(275.11, 373.43) * mm, v(276.63, 373.43) * mm]});
            skFitSpline(sketch, "E283", {"points": [v(276.63, 373.43) * mm, v(278.07, 373.43) * mm, v(279.73, 373.08) * mm, v(281.63, 372.4) * mm]});
            skFitSpline(sketch, "E284", {"points": [v(281.63, 372.4) * mm, v(280.16, 367.34) * mm, v(277.58, 364.81) * mm, v(273.88, 364.81) * mm]});
            skFitSpline(sketch, "E285", {"points": [v(273.88, 364.81) * mm, v(272.36, 364.81) * mm, v(270.86, 365.22) * mm, v(269.35, 366.02) * mm]});
            skFitSpline(sketch, "E286", {"points": [v(269.35, 366.02) * mm, v(265.7, 364.5) * mm, v(262.72, 362.19) * mm, v(260.42, 359.13) * mm]});
            skFitSpline(sketch, "E287", {"points": [v(260.42, 359.13) * mm, v(258.12, 356.06) * mm, v(256.96, 352.8) * mm, v(256.96, 349.32) * mm]});
            skFitSpline(sketch, "E288", {"points": [v(256.96, 349.32) * mm, v(256.96, 346.25) * mm, v(258.1, 343.74) * mm, v(260.39, 341.8) * mm]});
            skFitSpline(sketch, "E289", {"points": [v(260.39, 341.8) * mm, v(262.67, 339.86) * mm, v(265.66, 338.88) * mm, v(269.4, 338.88) * mm]});
            skFitSpline(sketch, "E290", {"points": [v(269.4, 338.88) * mm, v(273.9, 338.88) * mm, v(278.46, 340.78) * mm, v(283.03, 344.56) * mm]});
            skFitSpline(sketch, "E291", {"points": [v(283.03, 344.56) * mm, v(287.61, 348.33) * mm, v(289.9, 352.03) * mm, v(289.9, 355.63) * mm]});
            skFitSpline(sketch, "E292", {"points": [v(289.9, 355.63) * mm, v(289.9, 357.33) * mm, v(289.16, 358.57) * mm, v(287.7, 359.33) * mm]});
            skFitSpline(sketch, "E293", {"points": [v(286.49, 359.8) * mm, v(285.1, 360.5) * mm, v(284.39, 361.54) * mm, v(284.39, 362.92) * mm]});
            skFitSpline(sketch, "E294", {"points": [v(284.39, 362.92) * mm, v(284.39, 364.24) * mm, v(284.98, 366.15) * mm, v(286.17, 368.6) * mm]});
            skFitSpline(sketch, "E295", {"points": [v(286.17, 368.6) * mm, v(289.42, 367.14) * mm, v(293.87, 366.41) * mm, v(299.52, 366.41) * mm]});
            skFitSpline(sketch, "E296", {"points": [v(299.52, 366.41) * mm, v(302.52, 366.41) * mm, v(305.82, 366.82) * mm, v(309.44, 367.62) * mm]});
            skFitSpline(sketch, "E297", {"points": [v(309.44, 367.62) * mm, v(308.5, 363.93) * mm, v(307.32, 361.5) * mm, v(305.9, 360.33) * mm]});
            skFitSpline(sketch, "E298", {"points": [v(305.9, 360.33) * mm, v(304.46, 359.17) * mm, v(302.3, 358.6) * mm, v(299.4, 358.6) * mm]});
            skFitSpline(sketch, "E299", {"points": [v(299.4, 358.6) * mm, v(298.84, 358.6) * mm, v(298.17, 358.64) * mm, v(297.4, 358.75) * mm]});
            skFitSpline(sketch, "E300", {"points": [v(297.4, 358.75) * mm, v(294.74, 350.17) * mm, v(293.41, 343.18) * mm, v(293.41, 337.77) * mm]});
            skFitSpline(sketch, "E301", {"points": [v(293.41, 337.77) * mm, v(293.41, 333.72) * mm, v(294.08, 330.44) * mm, v(295.4, 327.95) * mm]});
            skFitSpline(sketch, "E302", {"points": [v(295.4, 327.95) * mm, v(293.52, 325.82) * mm, v(291.53, 324.77) * mm, v(289.43, 324.77) * mm]});
            skFitSpline(sketch, "E303", {"points": [v(289.43, 324.77) * mm, v(287.44, 324.77) * mm, v(286.45, 326.37) * mm, v(286.45, 329.58) * mm]});
            skFitSpline(sketch, "E304", {"points": [v(286.45, 329.58) * mm, v(286.45, 332.7) * mm, v(287.06, 337.43) * mm, v(288.26, 343.75) * mm]});
            skFitSpline(sketch, "E305", {"points": [v(288.26, 343.75) * mm, v(282.52, 336.1) * mm, v(275.37, 332.25) * mm, v(266.85, 332.25) * mm]});
            skFitSpline(sketch, "E306", {"points": [v(266.85, 332.25) * mm, v(261.33, 332.25) * mm, v(256.9, 333.76) * mm, v(253.56, 336.78) * mm]});
            skFitSpline(sketch, "E307", {"points": [v(253.56, 336.78) * mm, v(250.21, 339.8) * mm, v(248.55, 343.84) * mm, v(248.55, 348.92) * mm]});
            skFitSpline(sketch, "E308", {"points": [v(248.55, 348.92) * mm, v(248.55, 358.85) * mm, v(254.08, 365.7) * mm, v(265.16, 369.52) * mm]});
            skFitSpline(sketch, "E309", {"points": [v(265.16, 369.52) * mm, v(261.45, 371.14) * mm, v(259.6, 374.46) * mm, v(259.6, 379.46) * mm]});
            skFitSpline(sketch, "E310", {"points": [v(259.6, 379.46) * mm, v(259.6, 383.85) * mm, v(261.34, 387.47) * mm, v(264.82, 390.34) * mm]});
            skFitSpline(sketch, "E311", {"points": [v(264.82, 390.34) * mm, v(268.3, 393.21) * mm, v(272.62, 394.65) * mm, v(277.79, 394.65) * mm]});
            skFitSpline(sketch, "E312", {"points": [v(322.46, 256.65) * mm, v(318.75, 256.65) * mm, v(315.44, 254.74) * mm, v(312.52, 250.93) * mm]});
            skFitSpline(sketch, "E313", {"points": [v(312.52, 250.93) * mm, v(309.6, 247.1) * mm, v(308.14, 242.74) * mm, v(308.14, 237.81) * mm]});
            skFitSpline(sketch, "E314", {"points": [v(308.14, 237.81) * mm, v(308.14, 234.3) * mm, v(309, 231.42) * mm, v(310.71, 229.2) * mm]});
            skFitSpline(sketch, "E315", {"points": [v(310.71, 229.2) * mm, v(312.42, 227) * mm, v(314.6, 225.9) * mm, v(317.27, 225.9) * mm]});
            skFitSpline(sketch, "E316", {"points": [v(317.27, 225.9) * mm, v(320.96, 225.9) * mm, v(324.15, 228.04) * mm, v(326.87, 232.3) * mm]});
            skFitSpline(sketch, "E317", {"points": [v(326.87, 232.3) * mm, v(329.59, 236.57) * mm, v(330.95, 241.7) * mm, v(330.95, 247.66) * mm]});
            skFitSpline(sketch, "E318", {"points": [v(330.95, 247.66) * mm, v(330.95, 249.7) * mm, v(330.7, 251.56) * mm, v(330.2, 253.23) * mm]});
            skFitSpline(sketch, "E319", {"points": [v(330.2, 253.23) * mm, v(328.41, 253.83) * mm, v(326.72, 254.85) * mm, v(325.1, 256.27) * mm]});
            skFitSpline(sketch, "E320", {"points": [v(325.1, 256.27) * mm, v(324.07, 256.52) * mm, v(323.19, 256.65) * mm, v(322.46, 256.65) * mm]});
            skFitSpline(sketch, "E321", {"points": [v(240.42, 260.48) * mm, v(237.51, 260.48) * mm, v(234.78, 258.67) * mm, v(232.23, 255.02) * mm]});
            skFitSpline(sketch, "E322", {"points": [v(232.23, 255.02) * mm, v(229.66, 251.38) * mm, v(228.07, 247.23) * mm, v(227.45, 242.57) * mm]});
            skFitSpline(sketch, "E323", {"points": [v(227.45, 242.57) * mm, v(231.63, 242.83) * mm, v(235.4, 244.32) * mm, v(238.7, 247.04) * mm]});
            skFitSpline(sketch, "E324", {"points": [v(238.7, 247.04) * mm, v(242.03, 249.75) * mm, v(243.69, 252.82) * mm, v(243.69, 256.28) * mm]});
            skFitSpline(sketch, "E325", {"points": [v(243.69, 256.28) * mm, v(243.69, 259.09) * mm, v(242.6, 260.48) * mm, v(240.42, 260.48) * mm]});
            skFitSpline(sketch, "E326", {"points": [v(241.3, 265.95) * mm, v(244.47, 265.95) * mm, v(247.04, 265.03) * mm, v(249, 263.18) * mm]});
            skFitSpline(sketch, "E327", {"points": [v(249, 263.18) * mm, v(250.95, 261.35) * mm, v(251.93, 258.88) * mm, v(251.93, 255.8) * mm]});
            skFitSpline(sketch, "E328", {"points": [v(251.93, 255.8) * mm, v(251.93, 250.86) * mm, v(249.33, 246.53) * mm, v(244.16, 242.8) * mm]});
            skFitSpline(sketch, "E329", {"points": [v(244.16, 242.8) * mm, v(238.99, 239.07) * mm, v(233.32, 237.2) * mm, v(227.17, 237.2) * mm]});
            skFitSpline(sketch, "E330", {"points": [v(227.17, 237.2) * mm, v(227.17, 230.65) * mm, v(229.8, 227.37) * mm, v(235.06, 227.37) * mm]});
            skFitSpline(sketch, "E331", {"points": [v(235.06, 227.37) * mm, v(239.89, 227.37) * mm, v(245.25, 230) * mm, v(251.17, 235.25) * mm]});
            skFitSpline(sketch, "E332", {"points": [v(251.17, 235.25) * mm, v(256.88, 240.3) * mm, v(262.17, 247.06) * mm, v(267.04, 255.52) * mm]});
            skFitSpline(sketch, "E333", {"points": [v(267.04, 255.52) * mm, v(267.04, 255.63) * mm, v(267.05, 255.74) * mm, v(267.05, 255.84) * mm]});
            skFitSpline(sketch, "E334", {"points": [v(267.05, 255.84) * mm, v(267.05, 257.15) * mm, v(266.66, 258.53) * mm, v(265.9, 260) * mm]});
            skFitSpline(sketch, "E335", {"points": [v(265.9, 260) * mm, v(268.75, 261.23) * mm, v(270.96, 261.84) * mm, v(272.57, 261.84) * mm]});
            skFitSpline(sketch, "E336", {"points": [v(272.57, 261.84) * mm, v(274.69, 261.84) * mm, v(275.75, 260.41) * mm, v(275.75, 257.56) * mm]});
            skFitSpline(sketch, "E337", {"points": [v(275.75, 257.56) * mm, v(275.75, 256.1) * mm, v(275.15, 252.22) * mm, v(273.96, 245.95) * mm]});
            skFitSpline(sketch, "E338", {"points": [v(272.03, 235.67) * mm, v(275.54, 245) * mm, v(279.56, 252.4) * mm, v(284.1, 257.82) * mm]});
            skFitSpline(sketch, "E339", {"points": [v(284.1, 257.82) * mm, v(288.64, 263.24) * mm, v(292.83, 265.95) * mm, v(296.65, 265.95) * mm]});
            skFitSpline(sketch, "E340", {"points": [v(296.65, 265.95) * mm, v(298.1, 265.95) * mm, v(299.37, 265.46) * mm, v(300.46, 264.5) * mm]});
            skFitSpline(sketch, "E341", {"points": [v(300.46, 264.5) * mm, v(301.56, 263.54) * mm, v(302.1, 262.34) * mm, v(302.1, 260.93) * mm]});
            skFitSpline(sketch, "E342", {"points": [v(302.1, 260.93) * mm, v(302.1, 258.85) * mm, v(300, 256.15) * mm, v(295.8, 252.85) * mm]});
            skFitSpline(sketch, "E343", {"points": [v(295.8, 252.85) * mm, v(294.79, 254.9) * mm, v(293.62, 255.93) * mm, v(292.3, 255.93) * mm]});
            skFitSpline(sketch, "E344", {"points": [v(292.3, 255.93) * mm, v(289.6, 255.93) * mm, v(286.03, 252.53) * mm, v(281.6, 245.7) * mm]});
            skFitSpline(sketch, "E345", {"points": [v(281.6, 245.7) * mm, v(278.8, 241.39) * mm, v(276.38, 236.93) * mm, v(274.32, 232.34) * mm]});
            skFitSpline(sketch, "E346", {"points": [v(274.32, 232.34) * mm, v(272.26, 227.76) * mm, v(271.23, 224.47) * mm, v(271.23, 222.48) * mm]});
            skLineSegment(sketch, "E347", {"start": v(273.96, 245.95) * mm, "end": v(272.03, 235.67) * mm});
            skLineSegment(sketch, "E348", {"start": v(272.03, 235.67) * mm, "end": v(273.96, 245.95) * mm});
            skFitSpline(sketch, "E349", {"points": [v(271.27, 221.52) * mm, v(269.31, 220.47) * mm, v(267.8, 219.95) * mm, v(266.72, 219.95) * mm]});
            skFitSpline(sketch, "E350", {"points": [v(266.72, 219.95) * mm, v(263.89, 219.95) * mm, v(262.46, 221.4) * mm, v(262.46, 224.27) * mm]});
            skFitSpline(sketch, "E351", {"points": [v(262.46, 224.27) * mm, v(262.46, 225.52) * mm, v(262.89, 228.56) * mm, v(263.72, 233.37) * mm]});
            skLineSegment(sketch, "E352", {"start": v(271.23, 222.48) * mm, "end": v(271.27, 221.52) * mm});
            skLineSegment(sketch, "E353", {"start": v(271.27, 221.52) * mm, "end": v(271.23, 222.48) * mm});
            skFitSpline(sketch, "E354", {"points": [v(265.47, 243.21) * mm, v(261.99, 237.94) * mm, v(257.98, 233.36) * mm, v(253.47, 229.48) * mm]});
            skFitSpline(sketch, "E355", {"points": [v(253.47, 229.48) * mm, v(246.07, 223.13) * mm, v(239.03, 219.95) * mm, v(232.34, 219.95) * mm]});
            skFitSpline(sketch, "E356", {"points": [v(232.34, 219.95) * mm, v(227.94, 219.95) * mm, v(224.47, 221.55) * mm, v(221.91, 224.73) * mm]});
            skFitSpline(sketch, "E357", {"points": [v(221.91, 224.73) * mm, v(219.35, 227.92) * mm, v(218.07, 232.24) * mm, v(218.07, 237.69) * mm]});
            skFitSpline(sketch, "E358", {"points": [v(218.07, 237.69) * mm, v(218.07, 245.46) * mm, v(220.34, 252.12) * mm, v(224.87, 257.65) * mm]});
            skFitSpline(sketch, "E359", {"points": [v(224.87, 257.65) * mm, v(229.4, 263.18) * mm, v(234.88, 265.95) * mm, v(241.3, 265.95) * mm]});
            skLineSegment(sketch, "E360", {"start": v(263.72, 233.37) * mm, "end": v(265.46, 243.12) * mm});
            skLineSegment(sketch, "E361", {"start": v(265.46, 243.12) * mm, "end": v(265.47, 243.21) * mm});
            skLineSegment(sketch, "E362", {"start": v(265.47, 243.21) * mm, "end": v(263.72, 233.37) * mm});
            skFitSpline(sketch, "E363", {"points": [v(321.7, 268.35) * mm, v(327.88, 267.8) * mm, v(332.88, 264.45) * mm, v(336.73, 258.33) * mm]});
            skFitSpline(sketch, "E364", {"points": [v(336.73, 258.33) * mm, v(340.37, 255.54) * mm, v(344.2, 254.14) * mm, v(348.24, 254.14) * mm]});
            skFitSpline(sketch, "E365", {"points": [v(348.24, 254.14) * mm, v(349.7, 254.14) * mm, v(351.28, 254.46) * mm, v(353, 255.14) * mm]});
            skFitSpline(sketch, "E366", {"points": [v(353, 255.14) * mm, v(352.25, 256.33) * mm, v(351.5, 257.44) * mm, v(350.72, 258.45) * mm]});
            skFitSpline(sketch, "E367", {"points": [v(350.72, 258.45) * mm, v(352.74, 260.55) * mm, v(354.74, 261.6) * mm, v(356.73, 261.6) * mm]});
            skFitSpline(sketch, "E368", {"points": [v(356.73, 261.6) * mm, v(358.54, 261.6) * mm, v(360, 260.73) * mm, v(361.14, 259) * mm]});
            skFitSpline(sketch, "E369", {"points": [v(361.14, 259) * mm, v(362.27, 257.26) * mm, v(363.63, 254) * mm, v(365.2, 249.2) * mm]});
            skFitSpline(sketch, "E370", {"points": [v(365.2, 249.2) * mm, v(367.64, 241.7) * mm, v(369.34, 235.1) * mm, v(370.3, 229.37) * mm]});
            skFitSpline(sketch, "E371", {"points": [v(370.3, 229.37) * mm, v(377.47, 242.97) * mm, v(381.38, 255.16) * mm, v(382.06, 265.95) * mm]});
            skFitSpline(sketch, "E372", {"points": [v(382.06, 265.95) * mm, v(387.06, 265.2) * mm, v(389.57, 263.4) * mm, v(389.57, 260.57) * mm]});
            skFitSpline(sketch, "E373", {"points": [v(389.57, 260.57) * mm, v(389.57, 257.95) * mm, v(387.72, 252.7) * mm, v(384.02, 244.83) * mm]});
            skFitSpline(sketch, "E374", {"points": [v(384.02, 244.83) * mm, v(380.32, 236.96) * mm, v(376.35, 229.75) * mm, v(372.1, 223.22) * mm]});
            skFitSpline(sketch, "E375", {"points": [v(372.1, 223.22) * mm, v(367.2, 215.7) * mm, v(362.28, 209.74) * mm, v(357.38, 205.33) * mm]});
            skFitSpline(sketch, "E376", {"points": [v(357.38, 205.33) * mm, v(352.47, 200.93) * mm, v(348.2, 198.73) * mm, v(344.57, 198.73) * mm]});
            skFitSpline(sketch, "E377", {"points": [v(344.57, 198.73) * mm, v(340.98, 198.73) * mm, v(339.18, 200.47) * mm, v(339.18, 203.94) * mm]});
            skFitSpline(sketch, "E378", {"points": [v(339.18, 203.94) * mm, v(339.18, 205.24) * mm, v(339.59, 206.91) * mm, v(340.38, 208.95) * mm]});
            skFitSpline(sketch, "E379", {"points": [v(340.38, 208.95) * mm, v(342.03, 208.07) * mm, v(343.73, 207.63) * mm, v(345.47, 207.63) * mm]});
            skFitSpline(sketch, "E380", {"points": [v(345.47, 207.63) * mm, v(352.03, 207.63) * mm, v(358.3, 212.46) * mm, v(364.27, 222.14) * mm]});
            skFitSpline(sketch, "E381", {"points": [v(364.27, 222.14) * mm, v(363.28, 228.86) * mm, v(361.54, 235.6) * mm, v(359.02, 242.38) * mm]});
            skFitSpline(sketch, "E382", {"points": [v(359.02, 242.38) * mm, v(357.95, 245.25) * mm, v(356.83, 247.88) * mm, v(355.67, 250.25) * mm]});
            skFitSpline(sketch, "E383", {"points": [v(355.67, 250.25) * mm, v(352.93, 248.72) * mm, v(350.19, 247.96) * mm, v(347.44, 247.96) * mm]});
            skFitSpline(sketch, "E384", {"points": [v(347.44, 247.96) * mm, v(344.78, 247.96) * mm, v(342.1, 248.56) * mm, v(339.4, 249.76) * mm]});
            skFitSpline(sketch, "E385", {"points": [v(339.4, 249.76) * mm, v(339.48, 249.66) * mm, v(339.5, 249.36) * mm, v(339.5, 248.87) * mm]});
            skFitSpline(sketch, "E386", {"points": [v(339.5, 248.87) * mm, v(339.5, 241.14) * mm, v(337.16, 234.38) * mm, v(332.49, 228.6) * mm]});
            skFitSpline(sketch, "E387", {"points": [v(332.49, 228.6) * mm, v(327.8, 222.83) * mm, v(322.3, 219.95) * mm, v(315.95, 219.95) * mm]});
            skFitSpline(sketch, "E388", {"points": [v(315.95, 219.95) * mm, v(311.1, 219.95) * mm, v(307.12, 221.7) * mm, v(304.05, 225.22) * mm]});
            skFitSpline(sketch, "E389", {"points": [v(304.05, 225.22) * mm, v(300.98, 228.72) * mm, v(299.44, 233.26) * mm, v(299.44, 238.82) * mm]});
            skFitSpline(sketch, "E390", {"points": [v(299.44, 238.82) * mm, v(299.44, 245.12) * mm, v(301.4, 250.58) * mm, v(305.33, 255.2) * mm]});
            skFitSpline(sketch, "E391", {"points": [v(305.33, 255.2) * mm, v(309.26, 259.81) * mm, v(313.9, 262.12) * mm, v(319.26, 262.12) * mm]});
            skFitSpline(sketch, "E392", {"points": [v(319.26, 262.12) * mm, v(320.1, 262.12) * mm, v(320.7, 262) * mm, v(321.06, 261.76) * mm]});
            skFitSpline(sketch, "E393", {"points": [v(321.06, 261.76) * mm, v(320.47, 262.26) * mm, v(320.19, 263) * mm, v(320.19, 263.94) * mm]});
            skFitSpline(sketch, "E394", {"points": [v(320.19, 263.94) * mm, v(320.19, 265.37) * mm, v(320.7, 266.85) * mm, v(321.7, 268.35) * mm]});
            skFitSpline(sketch, "E395", {"points": [v(190.94, 286.25) * mm, v(192.87, 286.25) * mm, v(193.84, 285.06) * mm, v(193.84, 282.68) * mm]});
            skFitSpline(sketch, "E396", {"points": [v(193.84, 282.68) * mm, v(193.84, 282.18) * mm, v(193.44, 279.75) * mm, v(192.63, 275.4) * mm]});
            skFitSpline(sketch, "E397", {"points": [v(186.62, 241.34) * mm, v(185.75, 236.5) * mm, v(185.32, 233.12) * mm, v(185.32, 231.22) * mm]});
            skFitSpline(sketch, "E398", {"points": [v(185.32, 231.22) * mm, v(185.32, 228.5) * mm, v(188.28, 227.13) * mm, v(194.21, 227.13) * mm]});
            skFitSpline(sketch, "E399", {"points": [v(194.21, 227.13) * mm, v(199.86, 227.13) * mm, v(206.02, 228.45) * mm, v(212.68, 231.08) * mm]});
            skFitSpline(sketch, "E400", {"points": [v(212.68, 231.08) * mm, v(211.84, 227.71) * mm, v(210.86, 225.39) * mm, v(209.73, 224.13) * mm]});
            skFitSpline(sketch, "E401", {"points": [v(209.73, 224.13) * mm, v(208.6, 222.84) * mm, v(205.85, 221.75) * mm, v(201.5, 220.86) * mm]});
            skFitSpline(sketch, "E402", {"points": [v(201.5, 220.86) * mm, v(197.16, 219.96) * mm, v(192.62, 219.5) * mm, v(187.87, 219.5) * mm]});
            skFitSpline(sketch, "E403", {"points": [v(187.87, 219.5) * mm, v(179.99, 219.5) * mm, v(176.05, 222.62) * mm, v(176.05, 228.83) * mm]});
            skFitSpline(sketch, "E404", {"points": [v(176.05, 228.83) * mm, v(176.05, 230.48) * mm, v(176.44, 233.54) * mm, v(177.24, 238.01) * mm]});
            skLineSegment(sketch, "E405", {"start": v(192.63, 275.4) * mm, "end": v(186.62, 241.34) * mm});
            skLineSegment(sketch, "E406", {"start": v(186.62, 241.34) * mm, "end": v(192.63, 275.4) * mm});
            skFitSpline(sketch, "E407", {"points": [v(184.03, 276.41) * mm, v(184.41, 278.6) * mm, v(184.6, 280.13) * mm, v(184.6, 281.03) * mm]});
            skFitSpline(sketch, "E408", {"points": [v(184.6, 281.03) * mm, v(184.6, 281.73) * mm, v(184.33, 282.67) * mm, v(183.79, 283.85) * mm]});
            skFitSpline(sketch, "E409", {"points": [v(183.79, 283.85) * mm, v(187.28, 285.45) * mm, v(189.66, 286.25) * mm, v(190.94, 286.25) * mm]});
            skLineSegment(sketch, "E410", {"start": v(177.24, 238.01) * mm, "end": v(184.03, 276.41) * mm});
            skLineSegment(sketch, "E411", {"start": v(184.03, 276.41) * mm, "end": v(177.24, 238.01) * mm});
            skFitSpline(sketch, "E412", {"points": [v(322.46, 256.65) * mm, v(318.75, 256.65) * mm, v(315.44, 254.74) * mm, v(312.52, 250.93) * mm]});
            skFitSpline(sketch, "E413", {"points": [v(312.52, 250.93) * mm, v(309.6, 247.1) * mm, v(308.14, 242.74) * mm, v(308.14, 237.81) * mm]});
            skFitSpline(sketch, "E414", {"points": [v(308.14, 237.81) * mm, v(308.14, 234.3) * mm, v(309, 231.42) * mm, v(310.71, 229.2) * mm]});
            skFitSpline(sketch, "E415", {"points": [v(310.71, 229.2) * mm, v(312.42, 227) * mm, v(314.6, 225.9) * mm, v(317.27, 225.9) * mm]});
            skFitSpline(sketch, "E416", {"points": [v(317.27, 225.9) * mm, v(320.96, 225.9) * mm, v(324.15, 228.04) * mm, v(326.87, 232.3) * mm]});
            skFitSpline(sketch, "E417", {"points": [v(326.87, 232.3) * mm, v(329.59, 236.57) * mm, v(330.95, 241.7) * mm, v(330.95, 247.66) * mm]});
            skFitSpline(sketch, "E418", {"points": [v(330.95, 247.66) * mm, v(330.95, 249.7) * mm, v(330.7, 251.56) * mm, v(330.2, 253.23) * mm]});
            skFitSpline(sketch, "E419", {"points": [v(330.2, 253.23) * mm, v(328.41, 253.83) * mm, v(326.72, 254.85) * mm, v(325.1, 256.27) * mm]});
            skFitSpline(sketch, "E420", {"points": [v(325.1, 256.27) * mm, v(324.07, 256.52) * mm, v(323.19, 256.65) * mm, v(322.46, 256.65) * mm]});
            skFitSpline(sketch, "E421", {"points": [v(240.42, 260.48) * mm, v(237.51, 260.48) * mm, v(234.78, 258.67) * mm, v(232.23, 255.02) * mm]});
            skFitSpline(sketch, "E422", {"points": [v(232.23, 255.02) * mm, v(229.66, 251.38) * mm, v(228.07, 247.23) * mm, v(227.45, 242.57) * mm]});
            skFitSpline(sketch, "E423", {"points": [v(227.45, 242.57) * mm, v(231.63, 242.83) * mm, v(235.4, 244.32) * mm, v(238.7, 247.04) * mm]});
            skFitSpline(sketch, "E424", {"points": [v(238.7, 247.04) * mm, v(242.03, 249.75) * mm, v(243.69, 252.82) * mm, v(243.69, 256.28) * mm]});
            skFitSpline(sketch, "E425", {"points": [v(243.69, 256.28) * mm, v(243.69, 259.09) * mm, v(242.6, 260.48) * mm, v(240.42, 260.48) * mm]});
            skFitSpline(sketch, "E426", {"points": [v(241.3, 265.95) * mm, v(244.47, 265.95) * mm, v(247.04, 265.03) * mm, v(249, 263.18) * mm]});
            skFitSpline(sketch, "E427", {"points": [v(249, 263.18) * mm, v(250.95, 261.35) * mm, v(251.93, 258.88) * mm, v(251.93, 255.8) * mm]});
            skFitSpline(sketch, "E428", {"points": [v(251.93, 255.8) * mm, v(251.93, 250.86) * mm, v(249.33, 246.53) * mm, v(244.16, 242.8) * mm]});
            skFitSpline(sketch, "E429", {"points": [v(244.16, 242.8) * mm, v(238.99, 239.07) * mm, v(233.32, 237.2) * mm, v(227.17, 237.2) * mm]});
            skFitSpline(sketch, "E430", {"points": [v(227.17, 237.2) * mm, v(227.17, 230.65) * mm, v(229.8, 227.37) * mm, v(235.06, 227.37) * mm]});
            skFitSpline(sketch, "E431", {"points": [v(235.06, 227.37) * mm, v(239.89, 227.37) * mm, v(245.25, 230) * mm, v(251.17, 235.25) * mm]});
            skFitSpline(sketch, "E432", {"points": [v(251.17, 235.25) * mm, v(256.88, 240.3) * mm, v(262.17, 247.06) * mm, v(267.04, 255.52) * mm]});
            skFitSpline(sketch, "E433", {"points": [v(267.04, 255.52) * mm, v(267.04, 255.63) * mm, v(267.05, 255.74) * mm, v(267.05, 255.84) * mm]});
            skFitSpline(sketch, "E434", {"points": [v(267.05, 255.84) * mm, v(267.05, 257.15) * mm, v(266.66, 258.53) * mm, v(265.9, 260) * mm]});
            skFitSpline(sketch, "E435", {"points": [v(265.9, 260) * mm, v(268.75, 261.23) * mm, v(270.96, 261.84) * mm, v(272.57, 261.84) * mm]});
            skFitSpline(sketch, "E436", {"points": [v(272.57, 261.84) * mm, v(274.69, 261.84) * mm, v(275.75, 260.41) * mm, v(275.75, 257.56) * mm]});
            skFitSpline(sketch, "E437", {"points": [v(275.75, 257.56) * mm, v(275.75, 256.1) * mm, v(275.15, 252.22) * mm, v(273.96, 245.95) * mm]});
            skFitSpline(sketch, "E438", {"points": [v(272.03, 235.67) * mm, v(275.54, 245) * mm, v(279.56, 252.4) * mm, v(284.1, 257.82) * mm]});
            skFitSpline(sketch, "E439", {"points": [v(284.1, 257.82) * mm, v(288.64, 263.24) * mm, v(292.83, 265.95) * mm, v(296.65, 265.95) * mm]});
            skFitSpline(sketch, "E440", {"points": [v(296.65, 265.95) * mm, v(298.1, 265.95) * mm, v(299.37, 265.46) * mm, v(300.46, 264.5) * mm]});
            skFitSpline(sketch, "E441", {"points": [v(300.46, 264.5) * mm, v(301.56, 263.54) * mm, v(302.1, 262.34) * mm, v(302.1, 260.93) * mm]});
            skFitSpline(sketch, "E442", {"points": [v(302.1, 260.93) * mm, v(302.1, 258.85) * mm, v(300, 256.15) * mm, v(295.8, 252.85) * mm]});
            skFitSpline(sketch, "E443", {"points": [v(295.8, 252.85) * mm, v(294.79, 254.9) * mm, v(293.62, 255.93) * mm, v(292.3, 255.93) * mm]});
            skFitSpline(sketch, "E444", {"points": [v(292.3, 255.93) * mm, v(289.6, 255.93) * mm, v(286.03, 252.53) * mm, v(281.6, 245.7) * mm]});
            skFitSpline(sketch, "E445", {"points": [v(281.6, 245.7) * mm, v(278.8, 241.39) * mm, v(276.38, 236.93) * mm, v(274.32, 232.34) * mm]});
            skFitSpline(sketch, "E446", {"points": [v(274.32, 232.34) * mm, v(272.26, 227.76) * mm, v(271.23, 224.47) * mm, v(271.23, 222.48) * mm]});
            skFitSpline(sketch, "E447", {"points": [v(271.27, 221.52) * mm, v(269.31, 220.47) * mm, v(267.8, 219.95) * mm, v(266.72, 219.95) * mm]});
            skFitSpline(sketch, "E448", {"points": [v(266.72, 219.95) * mm, v(263.89, 219.95) * mm, v(262.46, 221.4) * mm, v(262.46, 224.27) * mm]});
            skFitSpline(sketch, "E449", {"points": [v(262.46, 224.27) * mm, v(262.46, 225.52) * mm, v(262.89, 228.56) * mm, v(263.72, 233.37) * mm]});
            skFitSpline(sketch, "E450", {"points": [v(265.47, 243.21) * mm, v(261.99, 237.94) * mm, v(257.98, 233.36) * mm, v(253.47, 229.48) * mm]});
            skFitSpline(sketch, "E451", {"points": [v(253.47, 229.48) * mm, v(246.07, 223.13) * mm, v(239.03, 219.95) * mm, v(232.34, 219.95) * mm]});
            skFitSpline(sketch, "E452", {"points": [v(232.34, 219.95) * mm, v(227.94, 219.95) * mm, v(224.47, 221.55) * mm, v(221.91, 224.73) * mm]});
            skFitSpline(sketch, "E453", {"points": [v(221.91, 224.73) * mm, v(219.35, 227.92) * mm, v(218.07, 232.24) * mm, v(218.07, 237.69) * mm]});
            skFitSpline(sketch, "E454", {"points": [v(218.07, 237.69) * mm, v(218.07, 245.46) * mm, v(220.34, 252.12) * mm, v(224.87, 257.65) * mm]});
            skFitSpline(sketch, "E455", {"points": [v(224.87, 257.65) * mm, v(229.4, 263.18) * mm, v(234.88, 265.95) * mm, v(241.3, 265.95) * mm]});
            skFitSpline(sketch, "E456", {"points": [v(321.7, 268.35) * mm, v(327.88, 267.8) * mm, v(332.88, 264.45) * mm, v(336.73, 258.33) * mm]});
            skFitSpline(sketch, "E457", {"points": [v(336.73, 258.33) * mm, v(340.37, 255.54) * mm, v(344.2, 254.14) * mm, v(348.24, 254.14) * mm]});
            skFitSpline(sketch, "E458", {"points": [v(348.24, 254.14) * mm, v(349.7, 254.14) * mm, v(351.28, 254.46) * mm, v(353, 255.14) * mm]});
            skFitSpline(sketch, "E459", {"points": [v(353, 255.14) * mm, v(352.25, 256.33) * mm, v(351.5, 257.44) * mm, v(350.72, 258.45) * mm]});
            skFitSpline(sketch, "E460", {"points": [v(350.72, 258.45) * mm, v(352.74, 260.55) * mm, v(354.74, 261.6) * mm, v(356.73, 261.6) * mm]});
            skFitSpline(sketch, "E461", {"points": [v(356.73, 261.6) * mm, v(358.54, 261.6) * mm, v(360, 260.73) * mm, v(361.14, 259) * mm]});
            skFitSpline(sketch, "E462", {"points": [v(361.14, 259) * mm, v(362.27, 257.26) * mm, v(363.63, 254) * mm, v(365.2, 249.2) * mm]});
            skFitSpline(sketch, "E463", {"points": [v(365.2, 249.2) * mm, v(367.64, 241.7) * mm, v(369.34, 235.1) * mm, v(370.3, 229.37) * mm]});
            skFitSpline(sketch, "E464", {"points": [v(370.3, 229.37) * mm, v(377.47, 242.97) * mm, v(381.38, 255.16) * mm, v(382.06, 265.95) * mm]});
            skFitSpline(sketch, "E465", {"points": [v(382.06, 265.95) * mm, v(387.06, 265.2) * mm, v(389.57, 263.4) * mm, v(389.57, 260.57) * mm]});
            skFitSpline(sketch, "E466", {"points": [v(389.57, 260.57) * mm, v(389.57, 257.95) * mm, v(387.72, 252.7) * mm, v(384.02, 244.83) * mm]});
            skFitSpline(sketch, "E467", {"points": [v(384.02, 244.83) * mm, v(380.32, 236.96) * mm, v(376.35, 229.75) * mm, v(372.1, 223.22) * mm]});
            skFitSpline(sketch, "E468", {"points": [v(372.1, 223.22) * mm, v(367.2, 215.7) * mm, v(362.28, 209.74) * mm, v(357.38, 205.33) * mm]});
            skFitSpline(sketch, "E469", {"points": [v(357.38, 205.33) * mm, v(352.47, 200.93) * mm, v(348.2, 198.73) * mm, v(344.57, 198.73) * mm]});
            skFitSpline(sketch, "E470", {"points": [v(344.57, 198.73) * mm, v(340.98, 198.73) * mm, v(339.18, 200.47) * mm, v(339.18, 203.94) * mm]});
            skFitSpline(sketch, "E471", {"points": [v(339.18, 203.94) * mm, v(339.18, 205.24) * mm, v(339.59, 206.91) * mm, v(340.38, 208.95) * mm]});
            skFitSpline(sketch, "E472", {"points": [v(340.38, 208.95) * mm, v(342.03, 208.07) * mm, v(343.73, 207.63) * mm, v(345.47, 207.63) * mm]});
            skFitSpline(sketch, "E473", {"points": [v(345.47, 207.63) * mm, v(352.03, 207.63) * mm, v(358.3, 212.46) * mm, v(364.27, 222.14) * mm]});
            skFitSpline(sketch, "E474", {"points": [v(364.27, 222.14) * mm, v(363.28, 228.86) * mm, v(361.54, 235.6) * mm, v(359.02, 242.38) * mm]});
            skFitSpline(sketch, "E475", {"points": [v(359.02, 242.38) * mm, v(357.95, 245.25) * mm, v(356.83, 247.88) * mm, v(355.67, 250.25) * mm]});
            skFitSpline(sketch, "E476", {"points": [v(355.67, 250.25) * mm, v(352.93, 248.72) * mm, v(350.19, 247.96) * mm, v(347.44, 247.96) * mm]});
            skFitSpline(sketch, "E477", {"points": [v(347.44, 247.96) * mm, v(344.78, 247.96) * mm, v(342.1, 248.56) * mm, v(339.4, 249.76) * mm]});
            skFitSpline(sketch, "E478", {"points": [v(339.4, 249.76) * mm, v(339.48, 249.66) * mm, v(339.5, 249.36) * mm, v(339.5, 248.87) * mm]});
            skFitSpline(sketch, "E479", {"points": [v(339.5, 248.87) * mm, v(339.5, 241.14) * mm, v(337.16, 234.38) * mm, v(332.49, 228.6) * mm]});
            skFitSpline(sketch, "E480", {"points": [v(332.49, 228.6) * mm, v(327.8, 222.83) * mm, v(322.3, 219.95) * mm, v(315.95, 219.95) * mm]});
            skFitSpline(sketch, "E481", {"points": [v(315.95, 219.95) * mm, v(311.1, 219.95) * mm, v(307.12, 221.7) * mm, v(304.05, 225.22) * mm]});
            skFitSpline(sketch, "E482", {"points": [v(304.05, 225.22) * mm, v(300.98, 228.72) * mm, v(299.44, 233.26) * mm, v(299.44, 238.82) * mm]});
            skFitSpline(sketch, "E483", {"points": [v(299.44, 238.82) * mm, v(299.44, 245.12) * mm, v(301.4, 250.58) * mm, v(305.33, 255.2) * mm]});
            skFitSpline(sketch, "E484", {"points": [v(305.33, 255.2) * mm, v(309.26, 259.81) * mm, v(313.9, 262.12) * mm, v(319.26, 262.12) * mm]});
            skFitSpline(sketch, "E485", {"points": [v(319.26, 262.12) * mm, v(320.1, 262.12) * mm, v(320.7, 262) * mm, v(321.06, 261.76) * mm]});
            skFitSpline(sketch, "E486", {"points": [v(321.06, 261.76) * mm, v(320.47, 262.26) * mm, v(320.19, 263) * mm, v(320.19, 263.94) * mm]});
            skFitSpline(sketch, "E487", {"points": [v(320.19, 263.94) * mm, v(320.19, 265.37) * mm, v(320.7, 266.85) * mm, v(321.7, 268.35) * mm]});
            skFitSpline(sketch, "E488", {"points": [v(190.94, 286.25) * mm, v(192.87, 286.25) * mm, v(193.84, 285.06) * mm, v(193.84, 282.68) * mm]});
            skFitSpline(sketch, "E489", {"points": [v(193.84, 282.68) * mm, v(193.84, 282.18) * mm, v(193.44, 279.75) * mm, v(192.63, 275.4) * mm]});
            skFitSpline(sketch, "E490", {"points": [v(186.62, 241.34) * mm, v(185.75, 236.5) * mm, v(185.32, 233.12) * mm, v(185.32, 231.22) * mm]});
            skFitSpline(sketch, "E491", {"points": [v(185.32, 231.22) * mm, v(185.32, 228.5) * mm, v(188.28, 227.13) * mm, v(194.21, 227.13) * mm]});
            skFitSpline(sketch, "E492", {"points": [v(194.21, 227.13) * mm, v(199.86, 227.13) * mm, v(206.02, 228.45) * mm, v(212.68, 231.08) * mm]});
            skFitSpline(sketch, "E493", {"points": [v(212.68, 231.08) * mm, v(211.84, 227.71) * mm, v(210.86, 225.39) * mm, v(209.73, 224.13) * mm]});
            skFitSpline(sketch, "E494", {"points": [v(209.73, 224.13) * mm, v(208.6, 222.84) * mm, v(205.85, 221.75) * mm, v(201.5, 220.86) * mm]});
            skFitSpline(sketch, "E495", {"points": [v(201.5, 220.86) * mm, v(197.16, 219.96) * mm, v(192.62, 219.5) * mm, v(187.87, 219.5) * mm]});
            skFitSpline(sketch, "E496", {"points": [v(187.87, 219.5) * mm, v(179.99, 219.5) * mm, v(176.05, 222.62) * mm, v(176.05, 228.83) * mm]});
            skFitSpline(sketch, "E497", {"points": [v(176.05, 228.83) * mm, v(176.05, 230.48) * mm, v(176.44, 233.54) * mm, v(177.24, 238.01) * mm]});
            skFitSpline(sketch, "E498", {"points": [v(184.03, 276.41) * mm, v(184.41, 278.6) * mm, v(184.6, 280.13) * mm, v(184.6, 281.03) * mm]});
            skFitSpline(sketch, "E499", {"points": [v(184.6, 281.03) * mm, v(184.6, 281.73) * mm, v(184.33, 282.67) * mm, v(183.79, 283.85) * mm]});
            skFitSpline(sketch, "E500", {"points": [v(183.79, 283.85) * mm, v(187.28, 285.45) * mm, v(189.66, 286.25) * mm, v(190.94, 286.25) * mm]});
            skFitSpline(sketch, "E501", {"points": [v(148.9, 160.76) * mm, v(152.84, 160.76) * mm, v(156.03, 159.69) * mm, v(158.5, 157.52) * mm]});
            skFitSpline(sketch, "E502", {"points": [v(158.5, 157.52) * mm, v(160.96, 155.36) * mm, v(162.2, 152.5) * mm, v(162.2, 148.95) * mm]});
            skFitSpline(sketch, "E503", {"points": [v(162.2, 148.95) * mm, v(162.2, 139.05) * mm, v(152.73, 125.67) * mm, v(133.82, 108.83) * mm]});
            skFitSpline(sketch, "E504", {"points": [v(133.82, 108.83) * mm, v(141.2, 110.02) * mm, v(147.51, 110.62) * mm, v(152.72, 110.62) * mm]});
            skFitSpline(sketch, "E505", {"points": [v(152.72, 110.62) * mm, v(156.78, 110.62) * mm, v(159.46, 109.94) * mm, v(160.79, 108.57) * mm]});
            skFitSpline(sketch, "E506", {"points": [v(160.79, 108.57) * mm, v(162.11, 107.2) * mm, v(162.93, 103.95) * mm, v(163.25, 98.82) * mm]});
            skFitSpline(sketch, "E507", {"points": [v(163.25, 98.82) * mm, v(159.1, 100.65) * mm, v(154.02, 101.57) * mm, v(148.06, 101.57) * mm]});
            skFitSpline(sketch, "E508", {"points": [v(148.06, 101.57) * mm, v(143.16, 101.57) * mm, v(138.24, 101.13) * mm, v(133.32, 100.27) * mm]});
            skFitSpline(sketch, "E509", {"points": [v(131.2, 99.92) * mm, v(129.2, 99.58) * mm, v(127.89, 99.4) * mm, v(127.26, 99.4) * mm]});
            skFitSpline(sketch, "E510", {"points": [v(127.26, 99.4) * mm, v(125.1, 99.4) * mm, v(124.04, 100.8) * mm, v(124.04, 103.6) * mm]});
            skFitSpline(sketch, "E511", {"points": [v(124.04, 103.6) * mm, v(124.04, 104.4) * mm, v(124.14, 105.62) * mm, v(124.32, 107.24) * mm]});
            skFitSpline(sketch, "E512", {"points": [v(124.32, 107.24) * mm, v(132.32, 113.12) * mm, v(139.12, 119.9) * mm, v(144.71, 127.63) * mm]});
            skFitSpline(sketch, "E513", {"points": [v(144.71, 127.63) * mm, v(150.3, 135.35) * mm, v(153.1, 141.66) * mm, v(153.1, 146.57) * mm]});
            skFitSpline(sketch, "E514", {"points": [v(153.1, 146.57) * mm, v(153.1, 151.09) * mm, v(150.85, 153.34) * mm, v(146.35, 153.34) * mm]});
            skFitSpline(sketch, "E515", {"points": [v(146.35, 153.34) * mm, v(140.98, 153.34) * mm, v(135.91, 149.75) * mm, v(131.13, 142.53) * mm]});
            skFitSpline(sketch, "E516", {"points": [v(131.13, 142.53) * mm, v(130.6, 144.51) * mm, v(130.34, 146) * mm, v(130.34, 147.01) * mm]});
            skFitSpline(sketch, "E517", {"points": [v(130.34, 147.01) * mm, v(130.34, 150.43) * mm, v(132.32, 153.57) * mm, v(136.28, 156.45) * mm]});
            skFitSpline(sketch, "E518", {"points": [v(136.28, 156.45) * mm, v(140.24, 159.33) * mm, v(144.45, 160.76) * mm, v(148.9, 160.76) * mm]});
            skLineSegment(sketch, "E519", {"start": v(133.32, 100.27) * mm, "end": v(131.2, 99.92) * mm});
            skLineSegment(sketch, "E520", {"start": v(131.2, 99.92) * mm, "end": v(133.32, 100.27) * mm});
            skFitSpline(sketch, "E521", {"points": [v(148.9, 160.76) * mm, v(152.84, 160.76) * mm, v(156.03, 159.69) * mm, v(158.5, 157.52) * mm]});
            skFitSpline(sketch, "E522", {"points": [v(158.5, 157.52) * mm, v(160.96, 155.36) * mm, v(162.2, 152.5) * mm, v(162.2, 148.95) * mm]});
            skFitSpline(sketch, "E523", {"points": [v(162.2, 148.95) * mm, v(162.2, 139.05) * mm, v(152.73, 125.67) * mm, v(133.82, 108.83) * mm]});
            skFitSpline(sketch, "E524", {"points": [v(133.82, 108.83) * mm, v(141.2, 110.02) * mm, v(147.51, 110.62) * mm, v(152.72, 110.62) * mm]});
            skFitSpline(sketch, "E525", {"points": [v(152.72, 110.62) * mm, v(156.78, 110.62) * mm, v(159.46, 109.94) * mm, v(160.79, 108.57) * mm]});
            skFitSpline(sketch, "E526", {"points": [v(160.79, 108.57) * mm, v(162.11, 107.2) * mm, v(162.93, 103.95) * mm, v(163.25, 98.82) * mm]});
            skFitSpline(sketch, "E527", {"points": [v(163.25, 98.82) * mm, v(159.1, 100.65) * mm, v(154.02, 101.57) * mm, v(148.06, 101.57) * mm]});
            skFitSpline(sketch, "E528", {"points": [v(148.06, 101.57) * mm, v(143.16, 101.57) * mm, v(138.24, 101.13) * mm, v(133.32, 100.27) * mm]});
            skFitSpline(sketch, "E529", {"points": [v(131.2, 99.92) * mm, v(129.2, 99.58) * mm, v(127.89, 99.4) * mm, v(127.26, 99.4) * mm]});
            skFitSpline(sketch, "E530", {"points": [v(127.26, 99.4) * mm, v(125.1, 99.4) * mm, v(124.04, 100.8) * mm, v(124.04, 103.6) * mm]});
            skFitSpline(sketch, "E531", {"points": [v(124.04, 103.6) * mm, v(124.04, 104.4) * mm, v(124.14, 105.62) * mm, v(124.32, 107.24) * mm]});
            skFitSpline(sketch, "E532", {"points": [v(124.32, 107.24) * mm, v(132.32, 113.12) * mm, v(139.12, 119.9) * mm, v(144.71, 127.63) * mm]});
            skFitSpline(sketch, "E533", {"points": [v(144.71, 127.63) * mm, v(150.3, 135.35) * mm, v(153.1, 141.66) * mm, v(153.1, 146.57) * mm]});
            skFitSpline(sketch, "E534", {"points": [v(153.1, 146.57) * mm, v(153.1, 151.09) * mm, v(150.85, 153.34) * mm, v(146.35, 153.34) * mm]});
            skFitSpline(sketch, "E535", {"points": [v(146.35, 153.34) * mm, v(140.98, 153.34) * mm, v(135.91, 149.75) * mm, v(131.13, 142.53) * mm]});
            skFitSpline(sketch, "E536", {"points": [v(131.13, 142.53) * mm, v(130.6, 144.51) * mm, v(130.34, 146) * mm, v(130.34, 147.01) * mm]});
            skFitSpline(sketch, "E537", {"points": [v(130.34, 147.01) * mm, v(130.34, 150.43) * mm, v(132.32, 153.57) * mm, v(136.28, 156.45) * mm]});
            skFitSpline(sketch, "E538", {"points": [v(136.28, 156.45) * mm, v(140.24, 159.33) * mm, v(144.45, 160.76) * mm, v(148.9, 160.76) * mm]});
            skFitSpline(sketch, "E539", {"points": [v(202.2, 129.7) * mm, v(201.44, 123.52) * mm, v(199.56, 120.44) * mm, v(196.58, 120.44) * mm]});
            skFitSpline(sketch, "E540", {"points": [v(196.58, 120.44) * mm, v(195.93, 120.44) * mm, v(195.18, 120.5) * mm, v(194.33, 120.6) * mm]});
            skFitSpline(sketch, "E541", {"points": [v(191.57, 120.98) * mm, v(189.87, 121.23) * mm, v(188.55, 121.35) * mm, v(187.62, 121.35) * mm]});
            skFitSpline(sketch, "E542", {"points": [v(187.62, 121.35) * mm, v(186.31, 121.35) * mm, v(184.66, 120.96) * mm, v(182.65, 120.15) * mm]});
            skFitSpline(sketch, "E543", {"points": [v(182.65, 120.15) * mm, v(184.1, 125.83) * mm, v(186.47, 128.65) * mm, v(189.74, 128.65) * mm]});
            skFitSpline(sketch, "E544", {"points": [v(189.74, 128.65) * mm, v(190.3, 128.65) * mm, v(190.9, 128.6) * mm, v(191.57, 128.53) * mm]});
            skLineSegment(sketch, "E545", {"start": v(194.33, 120.6) * mm, "end": v(191.57, 120.98) * mm});
            skLineSegment(sketch, "E546", {"start": v(191.57, 120.98) * mm, "end": v(194.33, 120.6) * mm});
            skFitSpline(sketch, "E547", {"points": [v(195.42, 128.04) * mm, v(196.04, 127.97) * mm, v(196.72, 127.94) * mm, v(197.45, 127.94) * mm]});
            skFitSpline(sketch, "E548", {"points": [v(197.45, 127.94) * mm, v(199.07, 127.94) * mm, v(200.66, 128.53) * mm, v(202.2, 129.7) * mm]});
            skLineSegment(sketch, "E549", {"start": v(191.57, 128.53) * mm, "end": v(195.42, 128.04) * mm});
            skLineSegment(sketch, "E550", {"start": v(195.42, 128.04) * mm, "end": v(191.57, 128.53) * mm});
            skFitSpline(sketch, "E551", {"points": [v(202.2, 129.7) * mm, v(201.44, 123.52) * mm, v(199.56, 120.44) * mm, v(196.58, 120.44) * mm]});
            skFitSpline(sketch, "E552", {"points": [v(196.58, 120.44) * mm, v(195.93, 120.44) * mm, v(195.18, 120.5) * mm, v(194.33, 120.6) * mm]});
            skFitSpline(sketch, "E553", {"points": [v(191.57, 120.98) * mm, v(189.87, 121.23) * mm, v(188.55, 121.35) * mm, v(187.62, 121.35) * mm]});
            skFitSpline(sketch, "E554", {"points": [v(187.62, 121.35) * mm, v(186.31, 121.35) * mm, v(184.66, 120.96) * mm, v(182.65, 120.15) * mm]});
            skFitSpline(sketch, "E555", {"points": [v(182.65, 120.15) * mm, v(184.1, 125.83) * mm, v(186.47, 128.65) * mm, v(189.74, 128.65) * mm]});
            skFitSpline(sketch, "E556", {"points": [v(189.74, 128.65) * mm, v(190.3, 128.65) * mm, v(190.9, 128.6) * mm, v(191.57, 128.53) * mm]});
            skFitSpline(sketch, "E557", {"points": [v(195.42, 128.04) * mm, v(196.04, 127.97) * mm, v(196.72, 127.94) * mm, v(197.45, 127.94) * mm]});
            skFitSpline(sketch, "E558", {"points": [v(197.45, 127.94) * mm, v(199.07, 127.94) * mm, v(200.66, 128.53) * mm, v(202.2, 129.7) * mm]});
            skFitSpline(sketch, "E559", {"points": [v(231.1, 107.4) * mm, v(233.12, 107.8) * mm, v(234.8, 107.99) * mm, v(236.16, 107.99) * mm]});
            skFitSpline(sketch, "E560", {"points": [v(236.16, 107.99) * mm, v(239.42, 107.99) * mm, v(241.64, 107.39) * mm, v(242.8, 106.17) * mm]});
            skFitSpline(sketch, "E561", {"points": [v(242.8, 106.17) * mm, v(243.98, 104.96) * mm, v(244.56, 102.4) * mm, v(244.56, 98.48) * mm]});
            skFitSpline(sketch, "E562", {"points": [v(244.56, 98.48) * mm, v(242.68, 99.4) * mm, v(240.77, 99.85) * mm, v(238.84, 99.85) * mm]});
            skFitSpline(sketch, "E563", {"points": [v(238.84, 99.85) * mm, v(236.6, 99.85) * mm, v(233.83, 99.62) * mm, v(230.56, 99.18) * mm]});
            skLineSegment(sketch, "E564", {"start": v(240.33, 160.84) * mm, "end": v(231.1, 107.4) * mm});
            skLineSegment(sketch, "E565", {"start": v(231.1, 107.4) * mm, "end": v(240.33, 160.84) * mm});
            skFitSpline(sketch, "E566", {"points": [v(225.68, 98.5) * mm, v(224.08, 98.26) * mm, v(221.9, 97.9) * mm, v(219.13, 97.41) * mm]});
            skFitSpline(sketch, "E567", {"points": [v(219.13, 97.41) * mm, v(218.25, 97.25) * mm, v(217.34, 97.17) * mm, v(216.4, 97.17) * mm]});
            skFitSpline(sketch, "E568", {"points": [v(216.4, 97.17) * mm, v(213.42, 97.17) * mm, v(211.7, 100.17) * mm, v(211.24, 106.14) * mm]});
            skFitSpline(sketch, "E569", {"points": [v(211.24, 106.14) * mm, v(213.04, 105.46) * mm, v(214.48, 105.12) * mm, v(215.58, 105.12) * mm]});
            skFitSpline(sketch, "E570", {"points": [v(215.58, 105.12) * mm, v(218.04, 105.12) * mm, v(220.36, 105.41) * mm, v(222.57, 106) * mm]});
            skLineSegment(sketch, "E571", {"start": v(230.56, 99.18) * mm, "end": v(225.68, 98.5) * mm});
            skLineSegment(sketch, "E572", {"start": v(225.68, 98.5) * mm, "end": v(230.56, 99.18) * mm});
            skFitSpline(sketch, "E573", {"points": [v(230.14, 148.1) * mm, v(226.91, 146) * mm, v(224.12, 144.93) * mm, v(221.77, 144.93) * mm]});
            skFitSpline(sketch, "E574", {"points": [v(221.77, 144.93) * mm, v(217.95, 144.93) * mm, v(216.04, 147.62) * mm, v(216.04, 153.01) * mm]});
            skLineSegment(sketch, "E575", {"start": v(222.57, 106) * mm, "end": v(230.14, 148.1) * mm});
            skLineSegment(sketch, "E576", {"start": v(230.14, 148.1) * mm, "end": v(222.57, 106) * mm});
            skFitSpline(sketch, "E577", {"points": [v(216.04, 154.9) * mm, v(218.1, 153.52) * mm, v(219.94, 152.83) * mm, v(221.59, 152.83) * mm]});
            skFitSpline(sketch, "E578", {"points": [v(221.59, 152.83) * mm, v(224.5, 152.83) * mm, v(229.56, 155.03) * mm, v(236.73, 159.44) * mm]});
            skFitSpline(sketch, "E579", {"points": [v(236.73, 159.44) * mm, v(237.05, 159.62) * mm, v(238.25, 160.1) * mm, v(240.33, 160.84) * mm]});
            skLineSegment(sketch, "E580", {"start": v(216.04, 153.01) * mm, "end": v(216.04, 154.9) * mm});
            skLineSegment(sketch, "E581", {"start": v(216.04, 154.9) * mm, "end": v(216.04, 153.01) * mm});
            skFitSpline(sketch, "E582", {"points": [v(231.1, 107.4) * mm, v(233.12, 107.8) * mm, v(234.8, 107.99) * mm, v(236.16, 107.99) * mm]});
            skFitSpline(sketch, "E583", {"points": [v(236.16, 107.99) * mm, v(239.42, 107.99) * mm, v(241.64, 107.39) * mm, v(242.8, 106.17) * mm]});
            skFitSpline(sketch, "E584", {"points": [v(242.8, 106.17) * mm, v(243.98, 104.96) * mm, v(244.56, 102.4) * mm, v(244.56, 98.48) * mm]});
            skFitSpline(sketch, "E585", {"points": [v(244.56, 98.48) * mm, v(242.68, 99.4) * mm, v(240.77, 99.85) * mm, v(238.84, 99.85) * mm]});
            skFitSpline(sketch, "E586", {"points": [v(238.84, 99.85) * mm, v(236.6, 99.85) * mm, v(233.83, 99.62) * mm, v(230.56, 99.18) * mm]});
            skFitSpline(sketch, "E587", {"points": [v(225.68, 98.5) * mm, v(224.08, 98.26) * mm, v(221.9, 97.9) * mm, v(219.13, 97.41) * mm]});
            skFitSpline(sketch, "E588", {"points": [v(219.13, 97.41) * mm, v(218.25, 97.25) * mm, v(217.34, 97.17) * mm, v(216.4, 97.17) * mm]});
            skFitSpline(sketch, "E589", {"points": [v(216.4, 97.17) * mm, v(213.42, 97.17) * mm, v(211.7, 100.17) * mm, v(211.24, 106.14) * mm]});
            skFitSpline(sketch, "E590", {"points": [v(211.24, 106.14) * mm, v(213.04, 105.46) * mm, v(214.48, 105.12) * mm, v(215.58, 105.12) * mm]});
            skFitSpline(sketch, "E591", {"points": [v(215.58, 105.12) * mm, v(218.04, 105.12) * mm, v(220.36, 105.41) * mm, v(222.57, 106) * mm]});
            skFitSpline(sketch, "E592", {"points": [v(230.14, 148.1) * mm, v(226.91, 146) * mm, v(224.12, 144.93) * mm, v(221.77, 144.93) * mm]});
            skFitSpline(sketch, "E593", {"points": [v(221.77, 144.93) * mm, v(217.95, 144.93) * mm, v(216.04, 147.62) * mm, v(216.04, 153.01) * mm]});
            skFitSpline(sketch, "E594", {"points": [v(216.04, 154.9) * mm, v(218.1, 153.52) * mm, v(219.94, 152.83) * mm, v(221.59, 152.83) * mm]});
            skFitSpline(sketch, "E595", {"points": [v(221.59, 152.83) * mm, v(224.5, 152.83) * mm, v(229.56, 155.03) * mm, v(236.73, 159.44) * mm]});
            skFitSpline(sketch, "E596", {"points": [v(236.73, 159.44) * mm, v(237.05, 159.62) * mm, v(238.25, 160.1) * mm, v(240.33, 160.84) * mm]});
            skFitSpline(sketch, "E597", {"points": [v(280.08, 107.4) * mm, v(282.1, 107.8) * mm, v(283.8, 107.99) * mm, v(285.15, 107.99) * mm]});
            skFitSpline(sketch, "E598", {"points": [v(285.15, 107.99) * mm, v(288.4, 107.99) * mm, v(290.62, 107.39) * mm, v(291.8, 106.17) * mm]});
            skFitSpline(sketch, "E599", {"points": [v(291.8, 106.17) * mm, v(292.97, 104.96) * mm, v(293.54, 102.4) * mm, v(293.54, 98.48) * mm]});
            skFitSpline(sketch, "E600", {"points": [v(293.54, 98.48) * mm, v(291.66, 99.4) * mm, v(289.75, 99.85) * mm, v(287.82, 99.85) * mm]});
            skFitSpline(sketch, "E601", {"points": [v(287.82, 99.85) * mm, v(285.58, 99.85) * mm, v(282.82, 99.62) * mm, v(279.55, 99.18) * mm]});
            skLineSegment(sketch, "E602", {"start": v(289.32, 160.84) * mm, "end": v(280.08, 107.4) * mm});
            skLineSegment(sketch, "E603", {"start": v(280.08, 107.4) * mm, "end": v(289.32, 160.84) * mm});
            skFitSpline(sketch, "E604", {"points": [v(274.67, 98.5) * mm, v(273.07, 98.26) * mm, v(270.89, 97.9) * mm, v(268.12, 97.41) * mm]});
            skFitSpline(sketch, "E605", {"points": [v(268.12, 97.41) * mm, v(267.24, 97.25) * mm, v(266.33, 97.17) * mm, v(265.4, 97.17) * mm]});
            skFitSpline(sketch, "E606", {"points": [v(265.4, 97.17) * mm, v(262.41, 97.17) * mm, v(260.68, 100.17) * mm, v(260.23, 106.14) * mm]});
            skFitSpline(sketch, "E607", {"points": [v(260.23, 106.14) * mm, v(262.03, 105.46) * mm, v(263.47, 105.12) * mm, v(264.56, 105.12) * mm]});
            skFitSpline(sketch, "E608", {"points": [v(264.56, 105.12) * mm, v(267.03, 105.12) * mm, v(269.35, 105.41) * mm, v(271.55, 106) * mm]});
            skLineSegment(sketch, "E609", {"start": v(279.55, 99.18) * mm, "end": v(274.67, 98.5) * mm});
            skLineSegment(sketch, "E610", {"start": v(274.67, 98.5) * mm, "end": v(279.55, 99.18) * mm});
            skFitSpline(sketch, "E611", {"points": [v(279.12, 148.1) * mm, v(275.9, 146) * mm, v(273.11, 144.93) * mm, v(270.76, 144.93) * mm]});
            skFitSpline(sketch, "E612", {"points": [v(270.76, 144.93) * mm, v(266.94, 144.93) * mm, v(265.03, 147.62) * mm, v(265.03, 153.01) * mm]});
            skLineSegment(sketch, "E613", {"start": v(271.55, 106) * mm, "end": v(279.12, 148.1) * mm});
            skLineSegment(sketch, "E614", {"start": v(279.12, 148.1) * mm, "end": v(271.55, 106) * mm});
            skFitSpline(sketch, "E615", {"points": [v(265.03, 154.9) * mm, v(267.08, 153.52) * mm, v(268.93, 152.83) * mm, v(270.57, 152.83) * mm]});
            skFitSpline(sketch, "E616", {"points": [v(270.57, 152.83) * mm, v(273.5, 152.83) * mm, v(278.55, 155.03) * mm, v(285.72, 159.44) * mm]});
            skFitSpline(sketch, "E617", {"points": [v(285.72, 159.44) * mm, v(286.03, 159.62) * mm, v(287.24, 160.1) * mm, v(289.32, 160.84) * mm]});
            skLineSegment(sketch, "E618", {"start": v(265.03, 153.01) * mm, "end": v(265.03, 154.9) * mm});
            skLineSegment(sketch, "E619", {"start": v(265.03, 154.9) * mm, "end": v(265.03, 153.01) * mm});
            skFitSpline(sketch, "E620", {"points": [v(280.08, 107.4) * mm, v(282.1, 107.8) * mm, v(283.8, 107.99) * mm, v(285.15, 107.99) * mm]});
            skFitSpline(sketch, "E621", {"points": [v(285.15, 107.99) * mm, v(288.4, 107.99) * mm, v(290.62, 107.39) * mm, v(291.8, 106.17) * mm]});
            skFitSpline(sketch, "E622", {"points": [v(291.8, 106.17) * mm, v(292.97, 104.96) * mm, v(293.54, 102.4) * mm, v(293.54, 98.48) * mm]});
            skFitSpline(sketch, "E623", {"points": [v(293.54, 98.48) * mm, v(291.66, 99.4) * mm, v(289.75, 99.85) * mm, v(287.82, 99.85) * mm]});
            skFitSpline(sketch, "E624", {"points": [v(287.82, 99.85) * mm, v(285.58, 99.85) * mm, v(282.82, 99.62) * mm, v(279.55, 99.18) * mm]});
            skFitSpline(sketch, "E625", {"points": [v(274.67, 98.5) * mm, v(273.07, 98.26) * mm, v(270.89, 97.9) * mm, v(268.12, 97.41) * mm]});
            skFitSpline(sketch, "E626", {"points": [v(268.12, 97.41) * mm, v(267.24, 97.25) * mm, v(266.33, 97.17) * mm, v(265.4, 97.17) * mm]});
            skFitSpline(sketch, "E627", {"points": [v(265.4, 97.17) * mm, v(262.41, 97.17) * mm, v(260.68, 100.17) * mm, v(260.23, 106.14) * mm]});
            skFitSpline(sketch, "E628", {"points": [v(260.23, 106.14) * mm, v(262.03, 105.46) * mm, v(263.47, 105.12) * mm, v(264.56, 105.12) * mm]});
            skFitSpline(sketch, "E629", {"points": [v(264.56, 105.12) * mm, v(267.03, 105.12) * mm, v(269.35, 105.41) * mm, v(271.55, 106) * mm]});
            skFitSpline(sketch, "E630", {"points": [v(279.12, 148.1) * mm, v(275.9, 146) * mm, v(273.11, 144.93) * mm, v(270.76, 144.93) * mm]});
            skFitSpline(sketch, "E631", {"points": [v(270.76, 144.93) * mm, v(266.94, 144.93) * mm, v(265.03, 147.62) * mm, v(265.03, 153.01) * mm]});
            skFitSpline(sketch, "E632", {"points": [v(265.03, 154.9) * mm, v(267.08, 153.52) * mm, v(268.93, 152.83) * mm, v(270.57, 152.83) * mm]});
            skFitSpline(sketch, "E633", {"points": [v(270.57, 152.83) * mm, v(273.5, 152.83) * mm, v(278.55, 155.03) * mm, v(285.72, 159.44) * mm]});
            skFitSpline(sketch, "E634", {"points": [v(285.72, 159.44) * mm, v(286.03, 159.62) * mm, v(287.24, 160.1) * mm, v(289.32, 160.84) * mm]});
            skFitSpline(sketch, "E635", {"points": [v(335.1, 129.7) * mm, v(334.33, 123.52) * mm, v(332.46, 120.44) * mm, v(329.47, 120.44) * mm]});
            skFitSpline(sketch, "E636", {"points": [v(329.47, 120.44) * mm, v(328.83, 120.44) * mm, v(328.08, 120.5) * mm, v(327.22, 120.6) * mm]});
            skFitSpline(sketch, "E637", {"points": [v(324.46, 120.98) * mm, v(322.76, 121.23) * mm, v(321.44, 121.35) * mm, v(320.51, 121.35) * mm]});
            skFitSpline(sketch, "E638", {"points": [v(320.51, 121.35) * mm, v(319.2, 121.35) * mm, v(317.55, 120.96) * mm, v(315.55, 120.15) * mm]});
            skFitSpline(sketch, "E639", {"points": [v(315.55, 120.15) * mm, v(317, 125.83) * mm, v(319.37, 128.65) * mm, v(322.63, 128.65) * mm]});
            skFitSpline(sketch, "E640", {"points": [v(322.63, 128.65) * mm, v(323.19, 128.65) * mm, v(323.8, 128.6) * mm, v(324.46, 128.53) * mm]});
            skLineSegment(sketch, "E641", {"start": v(327.22, 120.6) * mm, "end": v(324.46, 120.98) * mm});
            skLineSegment(sketch, "E642", {"start": v(324.46, 120.98) * mm, "end": v(327.22, 120.6) * mm});
            skFitSpline(sketch, "E643", {"points": [v(328.31, 128.04) * mm, v(328.94, 127.97) * mm, v(329.62, 127.94) * mm, v(330.34, 127.94) * mm]});
            skFitSpline(sketch, "E644", {"points": [v(330.34, 127.94) * mm, v(331.97, 127.94) * mm, v(333.56, 128.53) * mm, v(335.1, 129.7) * mm]});
            skLineSegment(sketch, "E645", {"start": v(324.46, 128.53) * mm, "end": v(328.31, 128.04) * mm});
            skLineSegment(sketch, "E646", {"start": v(328.31, 128.04) * mm, "end": v(324.46, 128.53) * mm});
            skFitSpline(sketch, "E647", {"points": [v(335.1, 129.7) * mm, v(334.33, 123.52) * mm, v(332.46, 120.44) * mm, v(329.47, 120.44) * mm]});
            skFitSpline(sketch, "E648", {"points": [v(329.47, 120.44) * mm, v(328.83, 120.44) * mm, v(328.08, 120.5) * mm, v(327.22, 120.6) * mm]});
            skFitSpline(sketch, "E649", {"points": [v(324.46, 120.98) * mm, v(322.76, 121.23) * mm, v(321.44, 121.35) * mm, v(320.51, 121.35) * mm]});
            skFitSpline(sketch, "E650", {"points": [v(320.51, 121.35) * mm, v(319.2, 121.35) * mm, v(317.55, 120.96) * mm, v(315.55, 120.15) * mm]});
            skFitSpline(sketch, "E651", {"points": [v(315.55, 120.15) * mm, v(317, 125.83) * mm, v(319.37, 128.65) * mm, v(322.63, 128.65) * mm]});
            skFitSpline(sketch, "E652", {"points": [v(322.63, 128.65) * mm, v(323.19, 128.65) * mm, v(323.8, 128.6) * mm, v(324.46, 128.53) * mm]});
            skFitSpline(sketch, "E653", {"points": [v(328.31, 128.04) * mm, v(328.94, 127.97) * mm, v(329.62, 127.94) * mm, v(330.34, 127.94) * mm]});
            skFitSpline(sketch, "E654", {"points": [v(330.34, 127.94) * mm, v(331.97, 127.94) * mm, v(333.56, 128.53) * mm, v(335.1, 129.7) * mm]});
            skFitSpline(sketch, "E655", {"points": [v(364.48, 107.4) * mm, v(366.5, 107.8) * mm, v(368.19, 107.99) * mm, v(369.54, 107.99) * mm]});
            skFitSpline(sketch, "E656", {"points": [v(369.54, 107.99) * mm, v(372.8, 107.99) * mm, v(375.02, 107.39) * mm, v(376.19, 106.17) * mm]});
            skFitSpline(sketch, "E657", {"points": [v(376.19, 106.17) * mm, v(377.36, 104.96) * mm, v(377.94, 102.4) * mm, v(377.94, 98.48) * mm]});
            skFitSpline(sketch, "E658", {"points": [v(377.94, 98.48) * mm, v(376.06, 99.4) * mm, v(374.15, 99.85) * mm, v(372.22, 99.85) * mm]});
            skFitSpline(sketch, "E659", {"points": [v(372.22, 99.85) * mm, v(369.97, 99.85) * mm, v(367.22, 99.62) * mm, v(363.94, 99.18) * mm]});
            skLineSegment(sketch, "E660", {"start": v(373.71, 160.84) * mm, "end": v(364.48, 107.4) * mm});
            skLineSegment(sketch, "E661", {"start": v(364.48, 107.4) * mm, "end": v(373.71, 160.84) * mm});
            skFitSpline(sketch, "E662", {"points": [v(359.06, 98.5) * mm, v(357.46, 98.26) * mm, v(355.28, 97.9) * mm, v(352.51, 97.41) * mm]});
            skFitSpline(sketch, "E663", {"points": [v(352.51, 97.41) * mm, v(351.63, 97.25) * mm, v(350.72, 97.17) * mm, v(349.78, 97.17) * mm]});
            skFitSpline(sketch, "E664", {"points": [v(349.78, 97.17) * mm, v(346.8, 97.17) * mm, v(345.08, 100.17) * mm, v(344.62, 106.14) * mm]});
            skFitSpline(sketch, "E665", {"points": [v(344.62, 106.14) * mm, v(346.42, 105.46) * mm, v(347.86, 105.12) * mm, v(348.96, 105.12) * mm]});
            skFitSpline(sketch, "E666", {"points": [v(348.96, 105.12) * mm, v(351.42, 105.12) * mm, v(353.75, 105.41) * mm, v(355.95, 106) * mm]});
            skLineSegment(sketch, "E667", {"start": v(363.94, 99.18) * mm, "end": v(359.06, 98.5) * mm});
            skLineSegment(sketch, "E668", {"start": v(359.06, 98.5) * mm, "end": v(363.94, 99.18) * mm});
            skFitSpline(sketch, "E669", {"points": [v(363.52, 148.1) * mm, v(360.3, 146) * mm, v(357.5, 144.93) * mm, v(355.15, 144.93) * mm]});
            skFitSpline(sketch, "E670", {"points": [v(355.15, 144.93) * mm, v(351.33, 144.93) * mm, v(349.42, 147.62) * mm, v(349.42, 153.01) * mm]});
            skLineSegment(sketch, "E671", {"start": v(355.95, 106) * mm, "end": v(363.52, 148.1) * mm});
            skLineSegment(sketch, "E672", {"start": v(363.52, 148.1) * mm, "end": v(355.95, 106) * mm});
            skFitSpline(sketch, "E673", {"points": [v(349.42, 154.9) * mm, v(351.47, 153.52) * mm, v(353.32, 152.83) * mm, v(354.97, 152.83) * mm]});
            skFitSpline(sketch, "E674", {"points": [v(354.97, 152.83) * mm, v(357.89, 152.83) * mm, v(362.94, 155.03) * mm, v(370.12, 159.44) * mm]});
            skFitSpline(sketch, "E675", {"points": [v(370.12, 159.44) * mm, v(370.43, 159.62) * mm, v(371.63, 160.1) * mm, v(373.71, 160.84) * mm]});
            skLineSegment(sketch, "E676", {"start": v(349.42, 153.01) * mm, "end": v(349.42, 154.9) * mm});
            skLineSegment(sketch, "E677", {"start": v(349.42, 154.9) * mm, "end": v(349.42, 153.01) * mm});
            skFitSpline(sketch, "E678", {"points": [v(399.53, 161.29) * mm, v(401.74, 160.06) * mm, v(404.75, 159.45) * mm, v(408.55, 159.45) * mm]});
            skFitSpline(sketch, "E679", {"points": [v(432.57, 150.65) * mm, v(425.06, 143.33) * mm, v(418.97, 135.14) * mm, v(414.28, 126.1) * mm]});
            skFitSpline(sketch, "E680", {"points": [v(414.28, 126.1) * mm, v(409.6, 117.05) * mm, v(407.25, 109.05) * mm, v(407.25, 102.1) * mm]});
            skFitSpline(sketch, "E681", {"points": [v(407.25, 102.1) * mm, v(407.25, 100.52) * mm, v(407.42, 98.58) * mm, v(407.77, 96.28) * mm]});
            skFitSpline(sketch, "E682", {"points": [v(407.77, 96.28) * mm, v(406.64, 95.93) * mm, v(405.75, 95.74) * mm, v(405.08, 95.74) * mm]});
            skFitSpline(sketch, "E683", {"points": [v(405.08, 95.74) * mm, v(400.09, 95.74) * mm, v(397.59, 97.79) * mm, v(397.59, 101.86) * mm]});
            skFitSpline(sketch, "E684", {"points": [v(397.59, 101.86) * mm, v(397.59, 104.73) * mm, v(398.72, 109.17) * mm, v(401, 115.15) * mm]});
            skFitSpline(sketch, "E685", {"points": [v(401, 115.15) * mm, v(403.29, 121.13) * mm, v(405.8, 126.31) * mm, v(408.57, 130.72) * mm]});
            skFitSpline(sketch, "E686", {"points": [v(408.57, 130.72) * mm, v(414.11, 139.56) * mm, v(419.76, 146.08) * mm, v(425.54, 150.28) * mm]});
            skLineSegment(sketch, "E687", {"start": v(408.55, 159.45) * mm, "end": v(410.1, 159.48) * mm});
            skLineSegment(sketch, "E688", {"start": v(410.1, 159.48) * mm, "end": v(414.9, 159.4) * mm});
            skLineSegment(sketch, "E689", {"start": v(414.9, 159.4) * mm, "end": v(419.69, 159.33) * mm});
            skLineSegment(sketch, "E690", {"start": v(419.69, 159.33) * mm, "end": v(433.97, 159.33) * mm});
            skLineSegment(sketch, "E691", {"start": v(433.97, 159.33) * mm, "end": v(432.57, 150.65) * mm});
            skFitSpline(sketch, "E692", {"points": [v(411.55, 150.23) * mm, v(406.34, 150.23) * mm, v(402.84, 150.48) * mm, v(401.06, 150.98) * mm]});
            skFitSpline(sketch, "E693", {"points": [v(401.06, 150.98) * mm, v(399.28, 151.48) * mm, v(398.39, 152.65) * mm, v(398.39, 154.51) * mm]});
            skFitSpline(sketch, "E694", {"points": [v(398.39, 154.51) * mm, v(398.39, 155.11) * mm, v(398.47, 155.9) * mm, v(398.64, 156.83) * mm]});
            skFitSpline(sketch, "E695", {"points": [v(398.64, 156.83) * mm, v(398.73, 157.24) * mm, v(398.84, 157.8) * mm, v(398.98, 158.52) * mm]});
            skLineSegment(sketch, "E696", {"start": v(425.54, 150.28) * mm, "end": v(413.55, 150.28) * mm});
            skLineSegment(sketch, "E697", {"start": v(413.55, 150.28) * mm, "end": v(411.55, 150.23) * mm});
            skLineSegment(sketch, "E698", {"start": v(411.55, 150.23) * mm, "end": v(425.54, 150.28) * mm});
            skLineSegment(sketch, "E699", {"start": v(398.98, 158.52) * mm, "end": v(399.53, 161.29) * mm});
            skLineSegment(sketch, "E700", {"start": v(399.53, 161.29) * mm, "end": v(398.98, 158.52) * mm});
            skFitSpline(sketch, "E701", {"points": [v(364.48, 107.4) * mm, v(366.5, 107.8) * mm, v(368.19, 107.99) * mm, v(369.54, 107.99) * mm]});
            skFitSpline(sketch, "E702", {"points": [v(369.54, 107.99) * mm, v(372.8, 107.99) * mm, v(375.02, 107.39) * mm, v(376.19, 106.17) * mm]});
            skFitSpline(sketch, "E703", {"points": [v(376.19, 106.17) * mm, v(377.36, 104.96) * mm, v(377.94, 102.4) * mm, v(377.94, 98.48) * mm]});
            skFitSpline(sketch, "E704", {"points": [v(377.94, 98.48) * mm, v(376.06, 99.4) * mm, v(374.15, 99.85) * mm, v(372.22, 99.85) * mm]});
            skFitSpline(sketch, "E705", {"points": [v(372.22, 99.85) * mm, v(369.97, 99.85) * mm, v(367.22, 99.62) * mm, v(363.94, 99.18) * mm]});
            skFitSpline(sketch, "E706", {"points": [v(359.06, 98.5) * mm, v(357.46, 98.26) * mm, v(355.28, 97.9) * mm, v(352.51, 97.41) * mm]});
            skFitSpline(sketch, "E707", {"points": [v(352.51, 97.41) * mm, v(351.63, 97.25) * mm, v(350.72, 97.17) * mm, v(349.78, 97.17) * mm]});
            skFitSpline(sketch, "E708", {"points": [v(349.78, 97.17) * mm, v(346.8, 97.17) * mm, v(345.08, 100.17) * mm, v(344.62, 106.14) * mm]});
            skFitSpline(sketch, "E709", {"points": [v(344.62, 106.14) * mm, v(346.42, 105.46) * mm, v(347.86, 105.12) * mm, v(348.96, 105.12) * mm]});
            skFitSpline(sketch, "E710", {"points": [v(348.96, 105.12) * mm, v(351.42, 105.12) * mm, v(353.75, 105.41) * mm, v(355.95, 106) * mm]});
            skFitSpline(sketch, "E711", {"points": [v(363.52, 148.1) * mm, v(360.3, 146) * mm, v(357.5, 144.93) * mm, v(355.15, 144.93) * mm]});
            skFitSpline(sketch, "E712", {"points": [v(355.15, 144.93) * mm, v(351.33, 144.93) * mm, v(349.42, 147.62) * mm, v(349.42, 153.01) * mm]});
            skFitSpline(sketch, "E713", {"points": [v(349.42, 154.9) * mm, v(351.47, 153.52) * mm, v(353.32, 152.83) * mm, v(354.97, 152.83) * mm]});
            skFitSpline(sketch, "E714", {"points": [v(354.97, 152.83) * mm, v(357.89, 152.83) * mm, v(362.94, 155.03) * mm, v(370.12, 159.44) * mm]});
            skFitSpline(sketch, "E715", {"points": [v(370.12, 159.44) * mm, v(370.43, 159.62) * mm, v(371.63, 160.1) * mm, v(373.71, 160.84) * mm]});
            skFitSpline(sketch, "E716", {"points": [v(399.53, 161.29) * mm, v(401.74, 160.06) * mm, v(404.75, 159.45) * mm, v(408.55, 159.45) * mm]});
            skFitSpline(sketch, "E717", {"points": [v(432.57, 150.65) * mm, v(425.06, 143.33) * mm, v(418.97, 135.14) * mm, v(414.28, 126.1) * mm]});
            skFitSpline(sketch, "E718", {"points": [v(414.28, 126.1) * mm, v(409.6, 117.05) * mm, v(407.25, 109.05) * mm, v(407.25, 102.1) * mm]});
            skFitSpline(sketch, "E719", {"points": [v(407.25, 102.1) * mm, v(407.25, 100.52) * mm, v(407.42, 98.58) * mm, v(407.77, 96.28) * mm]});
            skFitSpline(sketch, "E720", {"points": [v(407.77, 96.28) * mm, v(406.64, 95.93) * mm, v(405.75, 95.74) * mm, v(405.08, 95.74) * mm]});
            skFitSpline(sketch, "E721", {"points": [v(405.08, 95.74) * mm, v(400.09, 95.74) * mm, v(397.59, 97.79) * mm, v(397.59, 101.86) * mm]});
            skFitSpline(sketch, "E722", {"points": [v(397.59, 101.86) * mm, v(397.59, 104.73) * mm, v(398.72, 109.17) * mm, v(401, 115.15) * mm]});
            skFitSpline(sketch, "E723", {"points": [v(401, 115.15) * mm, v(403.29, 121.13) * mm, v(405.8, 126.31) * mm, v(408.57, 130.72) * mm]});
            skFitSpline(sketch, "E724", {"points": [v(408.57, 130.72) * mm, v(414.11, 139.56) * mm, v(419.76, 146.08) * mm, v(425.54, 150.28) * mm]});
            skFitSpline(sketch, "E725", {"points": [v(411.55, 150.23) * mm, v(406.34, 150.23) * mm, v(402.84, 150.48) * mm, v(401.06, 150.98) * mm]});
            skFitSpline(sketch, "E726", {"points": [v(401.06, 150.98) * mm, v(399.28, 151.48) * mm, v(398.39, 152.65) * mm, v(398.39, 154.51) * mm]});
            skFitSpline(sketch, "E727", {"points": [v(398.39, 154.51) * mm, v(398.39, 155.11) * mm, v(398.47, 155.9) * mm, v(398.64, 156.83) * mm]});
            skFitSpline(sketch, "E728", {"points": [v(398.64, 156.83) * mm, v(398.73, 157.24) * mm, v(398.84, 157.8) * mm, v(398.98, 158.52) * mm]});
            skLineSegment(sketch, "E729", {"start": v(279.4, 609.6) * mm, "end": v(278.58, 0) * mm, "construction": true});
            skArc(sketch, "E730.filletArc", {"start": v(188.28, 472.56) * mm, "mid": v(187.45, 473) * mm, "end": v(186.79, 472.34) * mm});
            skArc(sketch, "E731.filletArc", {"start": v(188.41, 480.96) * mm, "mid": v(188.8, 480.14) * mm, "end": v(189.7, 480.21) * mm});
            skArc(sketch, "E732.filletArc", {"start": v(194.75, 478.46) * mm, "mid": v(194.46, 478.01) * mm, "end": v(194.52, 477.48) * mm});
            skArc(sketch, "E733.filletArc", {"start": v(257.1, 465.34) * mm, "mid": v(256.47, 466.14) * mm, "end": v(255.57, 465.67) * mm});
            skArc(sketch, "E734.filletArc", {"start": v(286.88, 464.2) * mm, "mid": v(286.6, 464.62) * mm, "end": v(286.13, 464.48) * mm});
            skArc(sketch, "E735.filletArc", {"start": v(349.2, 459.96) * mm, "mid": v(348.89, 460.32) * mm, "end": v(348.44, 460.16) * mm});
            skSolve(sketch);
        }
        {
            var Q0;
            Q0=qSketchRegion(id+"F2",true);
            extrude(context, id + "F3", {"entities" : qUnion([Q0]), "operationType" : NewBodyOperationType.REMOVE, "oppositeDirection" : true, "depth" : 4.76 * mm});
        }
        {
            var Q0;
            {var subQ0=sQuery(id+"F0.wireOp",EDGE,"E4.filletArc");var subQ1=sQuery(id+"F0.wireOp",EDGE,"E3.filletArc");var subQ2=sQuery(id+"F0.wireOp",EDGE,"E2.filletArc");var subQ3=sQuery(id+"F0.wireOp",EDGE,"E1.filletArc");var subQ4=sQuery(id+"F0.wireOp",EDGE,"E0.bottom");var subQ5=sQuery(id+"F0.wireOp",EDGE,"E0.right");var subQ6=sQuery(id+"F0.wireOp",EDGE,"E0.top");var subQ7=sQuery(id+"F0.wireOp",EDGE,"E0.left");Q0=makeQuery(id+"F3.boolean.opBoolean","SPLIT",FACE,{"disambiguationData":[TD([makeQuery(id+"F1.opExtrude","SWEPT_FACE",FACE,{"disambiguationData":[OSD([subQ4])]})])],"derivedFrom":makeQuery(id+"F1.opExtrude","CAP_FACE",FACE,{"disambiguationData":[OSD([subQ4,subQ6,subQ7,subQ5,subQ3,subQ2,subQ1,subQ0])],"isStart":false})});}
            var sketch = newSketch(context, id + "F4", { "sketchPlane" : qUnion([Q0])});
            skLineSegment(sketch, "E736.bottom", {"start": v(0, 531.47) * mm, "end": v(558.8, 531.47) * mm});
            skLineSegment(sketch, "E736.top", {"start": v(0, 420.34) * mm, "end": v(558.8, 420.34) * mm});
            skLineSegment(sketch, "E737.0", {"start": v(0, 12.7) * mm, "end": v(0, 420.34) * mm});
            skArc(sketch, "E738.0", {"start": v(0, 12.7) * mm, "mid": v(3.72, 3.72) * mm, "end": v(12.7, 0) * mm});
            skLineSegment(sketch, "E739.0", {"start": v(12.7, 0) * mm, "end": v(546.1, 0) * mm});
            skArc(sketch, "E740.0", {"start": v(546.1, 0) * mm, "mid": v(555.08, 3.72) * mm, "end": v(558.8, 12.7) * mm});
            skLineSegment(sketch, "E740.1", {"start": v(558.8, 12.7) * mm, "end": v(558.8, 420.34) * mm});
            skLineSegment(sketch, "E741.trimOffspring", {"start": v(0, 531.47) * mm, "end": v(0, 596.9) * mm});
            skLineSegment(sketch, "E742.trimOffspring", {"start": v(558.8, 531.47) * mm, "end": v(558.8, 596.9) * mm});
            skArc(sketch, "E743.0", {"start": v(12.7, 609.6) * mm, "mid": v(3.72, 605.88) * mm, "end": v(0, 596.9) * mm});
            skLineSegment(sketch, "E743.1", {"start": v(12.7, 609.6) * mm, "end": v(546.1, 609.6) * mm});
            skArc(sketch, "E744.0", {"start": v(558.8, 596.9) * mm, "mid": v(555.08, 605.88) * mm, "end": v(546.1, 609.6) * mm});
            skSolve(sketch);
        }
        {
            var Q0;
            Q0=qSketchRegion(id+"F4",true);
            extrude(context, id + "F5", {"entities" : qUnion([Q0]), "operationType" : NewBodyOperationType.REMOVE, "endBound" : BoundingType.THROUGH_ALL, "oppositeDirection" : true, "depth" : 25.4 * mm});
        }
        {
            var Q0;
            Q0=makeQuery(id+"F1.opExtrude","SWEPT_BODY",BODY,{"disambiguationData":[OSD([sQuery(id+"F0.wireOp",EDGE,"E0.bottom"),sQuery(id+"F0.wireOp",EDGE,"E0.top"),sQuery(id+"F0.wireOp",EDGE,"E0.left"),sQuery(id+"F0.wireOp",EDGE,"E0.right"),sQuery(id+"F0.wireOp",EDGE,"E1.filletArc"),sQuery(id+"F0.wireOp",EDGE,"E2.filletArc"),sQuery(id+"F0.wireOp",EDGE,"E3.filletArc"),sQuery(id+"F0.wireOp",EDGE,"E4.filletArc")])]});
            transform(context, id + "F6", {"entities" : qUnion([Q0]), "transformType" : TransformType.TRANSLATION_3D, "dx" : 0 * mm, "dy" : 0 * mm, "dz" : 0 * mm, "makeCopy" : true});
        }
        {
            var Q0;
            Q0=makeQuery(id+"F6.opPattern","COPY",BODY,{"derivedFrom":makeQuery(id+"F1.opExtrude","SWEPT_BODY",BODY,{"disambiguationData":[OSD([sQuery(id+"F0.wireOp",EDGE,"E0.bottom"),sQuery(id+"F0.wireOp",EDGE,"E0.top"),sQuery(id+"F0.wireOp",EDGE,"E0.left"),sQuery(id+"F0.wireOp",EDGE,"E0.right"),sQuery(id+"F0.wireOp",EDGE,"E1.filletArc"),sQuery(id+"F0.wireOp",EDGE,"E2.filletArc"),sQuery(id+"F0.wireOp",EDGE,"E3.filletArc"),sQuery(id+"F0.wireOp",EDGE,"E4.filletArc")])]}),"instanceName":"1"});
            deleteBodies(context, id + "F7", {"entities" : qUnion([Q0])});
        }
    });
